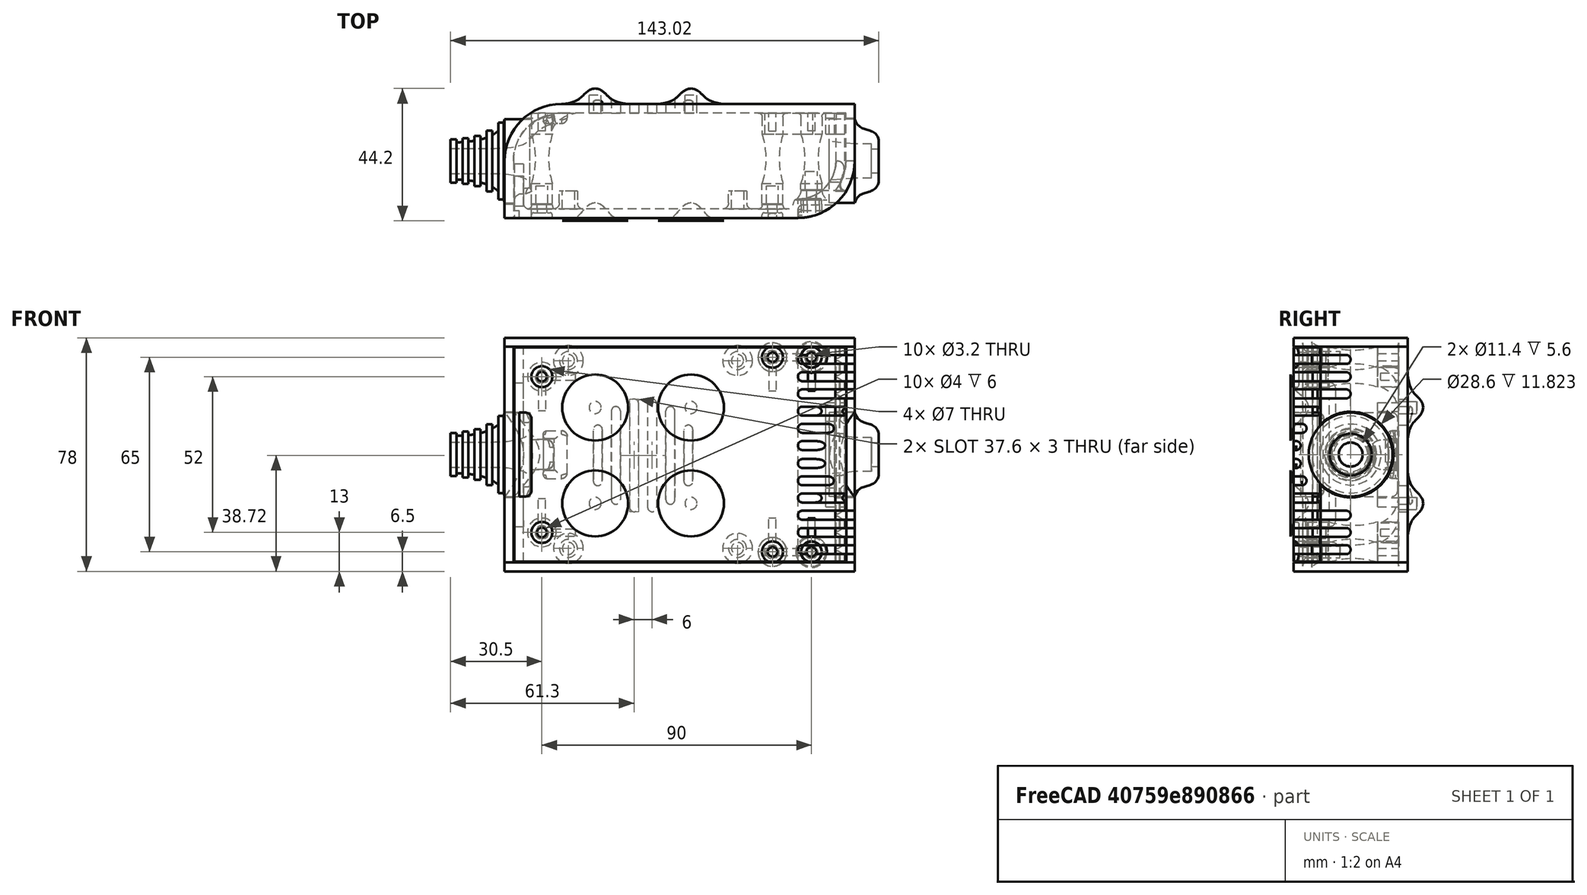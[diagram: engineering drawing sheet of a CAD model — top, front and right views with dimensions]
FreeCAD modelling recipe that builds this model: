
FCSTD DOCUMENT  (FreeCAD 0.19R0.19.2)
Label: enclosure_118
License: All rights reserved
LicenseURL: http://en.wikipedia.org/wiki/All_rights_reserved
objects: Part::Feature×72, Part::Revolution×72, Part::MultiFuse×53, Sketcher::SketchObject×32, Part::Fillet×24, Part::Cut×22, Part::Cylinder×22, Part::Extrusion×21, Part::Box×12, App::MeasureDistance×4
note: 330 computed .brp shape members not serialized (recipe doc carries the construction recipe); baked Part::Feature solids carry a one-line shape summary decoded from their .brp

FEATURE [Sketcher::SketchObject] Sketch  label="topSketch"
  FullyConstrained = true
  sketch-geometry (13):
    g0: LineSegment StartX=117 StartY=19 StartZ=0 EndX=117 EndY=38 EndZ=0
    g1: ArcOfCircle CenterX=98 CenterY=19 CenterZ=0 NormalX=0 NormalY=0 NormalZ=1 AngleXU=0 Radius=19 StartAngle=5.7297 EndAngle=6.28319
    g2: LineSegment StartX=0 StartY=3 StartZ=0 EndX=0 EndY=19 EndZ=0
    g3: LineSegment StartX=19 StartY=38 StartZ=0 EndX=117 EndY=38 EndZ=0
    g4: ArcOfCircle CenterX=19 CenterY=19 CenterZ=0 NormalX=0 NormalY=0 NormalZ=1 AngleXU=0 Radius=19 StartAngle=1.5708 EndAngle=3.14159
    g5: ArcOfCircle CenterX=19 CenterY=19 CenterZ=0 NormalX=0 NormalY=0 NormalZ=1 AngleXU=0 Radius=16 StartAngle=1.5708 EndAngle=3.14159
    g6: ArcOfCircle CenterX=98 CenterY=19 CenterZ=0 NormalX=0 NormalY=0 NormalZ=1 AngleXU=0 Radius=16 StartAngle=5.60905 EndAngle=6.28319
    g7: LineSegment StartX=114 StartY=19 StartZ=0 EndX=114 EndY=35 EndZ=0
    g8: LineSegment StartX=110.5 StartY=9.01251 StartZ=0 EndX=114.163 EndY=9.01251 EndZ=0
    g9: LineSegment StartX=114 StartY=35 StartZ=0 EndX=19 EndY=35 EndZ=0
    g10: LineSegment StartX=0 StartY=3 StartZ=0 EndX=0 EndY=0 EndZ=0
    g11: LineSegment StartX=3 StartY=0 StartZ=0 EndX=0 EndY=0 EndZ=0
    g12: LineSegment StartX=3 StartY=19 StartZ=0 EndX=3 EndY=0 EndZ=0
  constraints (33):
    c: Vertical(g0)
    c: Distance(g0) = 19
    c: Block(g0)
    c: Coincident(g1,g0)
    c: Block(g1)
    c: Vertical(g2)
    c: Block(g2)
    c: Coincident(g3,g0)
    c: Horizontal(g3)
    c: Distance(g3) = 98
    c: Coincident(g4,g3)
    c: Coincident(g4,g2)
    c: Block(g4)
    c: Coincident(g5,g4)
    c: Coincident(g6,g1)
    c: Block(g6)
    c: Block(g5)
    c: Coincident(g7,g6)
    c: Vertical(g7)
    c: Coincident(g8,g6)
    c: Coincident(g8,g1)
    c: Coincident(g9,g7)
    c: Coincident(g9,g5)
    c: Horizontal(g9)
    c: Tangent(g9,g5)
    c: Coincident(g10,g2)
    c: Distance(g10) = 3
    c: Vertical(g10)
    c: Coincident(g11,g10)
    c: Horizontal(g11)
    c: Coincident(g12,g5)
    c: Coincident(g12,g11)
    c: Vertical(g12)
FEATURE [Sketcher::SketchObject] Sketch001  label="bottomSketch"
  FullyConstrained = true
  sketch-geometry (32):
    g0: LineSegment StartX=3.3 StartY=-6.03275e-07 StartZ=0 EndX=98 EndY=-6.03275e-07 EndZ=0
    g1: ArcOfCircle CenterX=98 CenterY=19 CenterZ=0 NormalX=0 NormalY=0 NormalZ=1 AngleXU=0 Radius=19 StartAngle=4.71239 EndAngle=5.71103
    g2: LineSegment StartX=6.3 StartY=8 StartZ=0 EndX=3.3 EndY=8 EndZ=0
    g3: LineSegment StartX=3.3 StartY=8 StartZ=0 EndX=3.3 EndY=-6.03275e-07 EndZ=0
    g4: ArcOfCircle CenterX=8.3 CenterY=5 CenterZ=0 NormalX=0 NormalY=0 NormalZ=1 AngleXU=0 Radius=2 StartAngle=3.14159 EndAngle=4.71239
    g5: LineSegment StartX=6.3 StartY=8 StartZ=0 EndX=6.3 EndY=5 EndZ=0
    g6: ArcOfCircle CenterX=98 CenterY=19 CenterZ=0 NormalX=0 NormalY=0 NormalZ=1 AngleXU=0 Radius=12.7 StartAngle=4.71239 EndAngle=6.28319
    g7: LineSegment StartX=94.7 StartY=3 StartZ=0 EndX=8.3 EndY=3 EndZ=0
    g8-g12: Circle x5 (B-spline internal-alignment scaffolding for g13; pole/knot coordinates omitted)
    g13: BSplineCurve PolesCount=5 KnotsCount=3 Degree=3 IsPeriodic=0
    g14: GeomPoint X=98 Y=6.3 Z=0
    g15: GeomPoint X=96.3938 Y=4.71946 Z=0
    g16: GeomPoint X=94.7 Y=3 Z=0
    g17-g23: Circle x7 (B-spline internal-alignment scaffolding for g24; pole/knot coordinates omitted)
    g24: BSplineCurve PolesCount=7 KnotsCount=5 Degree=3 IsPeriodic=0
    g25-g29: GeomPoint x5 (B-spline internal-alignment scaffolding for g24; pole/knot coordinates omitted)
    g30: ArcOfCircle CenterX=98 CenterY=19 CenterZ=0 NormalX=0 NormalY=0 NormalZ=1 AngleXU=0 Radius=15.7 StartAngle=5.81226 EndAngle=6.28319
    g31: LineSegment StartX=110.7 StartY=19 StartZ=0 EndX=113.7 EndY=19 EndZ=0
  constraints (41):
    c: Horizontal(g0)
    c: Coincident(g1,g0)
    c: Block(g1)
    c: Horizontal(g2)
    c: Distance(g2) = 3
    c: Coincident(g3,g2)
    c: Vertical(g3)
    c: Coincident(g3,g0)
    c: Block(g4)
    c: Block(g2)
    c: Coincident(g5,g2)
    c: Coincident(g5,g4)
    c: Vertical(g5)
    c: Coincident(g6,g1)
    c: Block(g6)
    c: Coincident(g7,g4)
    c: Horizontal(g7)
    c: Block(g0)
    c: Block(g7)
    c: Block(g3)
    c: Coincident(g13,g6)
    c: Weight(g8) = 1
    c: Equal(g8, g9-g12) x4
    c: Coincident(g13,g7)
    c: InternalAlignment(g8-g12 -> g13) x5
    c: InternalAlignment(g14,g13)
    c: InternalAlignment(g15,g13)
    c: InternalAlignment(g16,g13)
    c: Block(g13)
    c: Weight(g17) = 1
    c: Equal(g17, g18-g23) x6
    c: Coincident(g24,g1)
    c: InternalAlignment(g17-g23 -> g24) x7
    c: InternalAlignment(g25-g29 -> g24) x5
    c: Block(g24)
    c: Coincident(g30,g24)
    c: Coincident(g31,g6)
    c: Coincident(g31,g30)
    c: Horizontal(g31)
    c: Block(g31)
    c: Block(g30)
FEATURE [Part::Extrusion] Extrude  label="top"
  Base = -> Sketch
  Dir = (0,0,1)
  DirMode = 2
  FaceMakerClass = Part::FaceMakerBullseye
  LengthFwd = 72
  LengthRev = 0
  Solid = true
  Symmetric = false
FEATURE [Part::Extrusion] Extrude001  label="bottom"
  Base = -> Sketch001
  Dir = (0,0,1)
  DirMode = 2
  FaceMakerClass = Part::FaceMakerBullseye
  LengthFwd = 71.4
  LengthRev = 0
  Placement = pos=(0,0,0.3) rot=(0,0,1;0rad)
  Solid = true
  Symmetric = false
FEATURE [Sketcher::SketchObject] Sketch002  label="topSketch001"
  FullyConstrained = true
  sketch-geometry (6):
    g0: LineSegment StartX=19 StartY=38 StartZ=0 EndX=117 EndY=38 EndZ=0
    g1: ArcOfCircle CenterX=19 CenterY=19 CenterZ=0 NormalX=0 NormalY=0 NormalZ=1 AngleXU=0 Radius=19 StartAngle=1.5708 EndAngle=3.14159
    g2: LineSegment StartX=117 StartY=38 StartZ=0 EndX=117 EndY=19 EndZ=0
    g3: LineSegment StartX=98 StartY=1.0161e-12 StartZ=0 EndX=5.22862e-06 EndY=1.0161e-12 EndZ=0
    g4: LineSegment StartX=5.22862e-06 StartY=19 StartZ=0 EndX=5.22862e-06 EndY=1.0161e-12 EndZ=0
    g5: ArcOfCircle CenterX=98 CenterY=19 CenterZ=0 NormalX=0 NormalY=0 NormalZ=1 AngleXU=0 Radius=19 StartAngle=4.71239 EndAngle=6.28319
  constraints (16):
    c: Horizontal(g0)
    c: Distance(g0) = 98
    c: Coincident(g1,g0)
    c: Block(g1)
    c: Coincident(g2,g0)
    c: Vertical(g2)
    c: Distance(g2) = 19
    c: Horizontal(g3)
    c: Coincident(g4,g1)
    c: Vertical(g4)
    c: Coincident(g3,g4)
    c: Block(g3)
    c: Coincident(g5,g2)
    c: Coincident(g5,g3)
    c: Block(g0)
    c: Block(g5)
FEATURE [Part::Extrusion] Extrude002  label="sideA"
  Base = -> Sketch002
  Dir = (0,0,1)
  DirMode = 2
  FaceMakerClass = Part::FaceMakerBullseye
  LengthFwd = 3
  LengthRev = 0
  Placement = pos=(0,0,-3) rot=(0,0,1;0rad)
  Solid = true
  Symmetric = false
FEATURE [Sketcher::SketchObject] Sketch003  label="topSketch002"
  FullyConstrained = true
  sketch-geometry (6):
    g0: LineSegment StartX=19 StartY=38 StartZ=0 EndX=117 EndY=38 EndZ=0
    g1: ArcOfCircle CenterX=19 CenterY=19 CenterZ=0 NormalX=0 NormalY=0 NormalZ=1 AngleXU=0 Radius=19 StartAngle=1.5708 EndAngle=3.14159
    g2: LineSegment StartX=117 StartY=38 StartZ=0 EndX=117 EndY=19 EndZ=0
    g3: LineSegment StartX=98 StartY=1.0161e-12 StartZ=0 EndX=5.22862e-06 EndY=1.0161e-12 EndZ=0
    g4: LineSegment StartX=5.22862e-06 StartY=19 StartZ=0 EndX=5.22862e-06 EndY=1.0161e-12 EndZ=0
    g5: ArcOfCircle CenterX=98 CenterY=19 CenterZ=0 NormalX=0 NormalY=0 NormalZ=1 AngleXU=0 Radius=19 StartAngle=4.71239 EndAngle=6.28319
  constraints (16):
    c: Horizontal(g0)
    c: Distance(g0) = 98
    c: Coincident(g1,g0)
    c: Block(g1)
    c: Coincident(g2,g0)
    c: Vertical(g2)
    c: Distance(g2) = 19
    c: Horizontal(g3)
    c: Coincident(g4,g1)
    c: Vertical(g4)
    c: Coincident(g3,g4)
    c: Block(g3)
    c: Coincident(g5,g2)
    c: Coincident(g5,g3)
    c: Block(g0)
    c: Block(g5)
FEATURE [Part::Extrusion] Extrude003  label="sideB"
  Base = -> Sketch003
  Dir = (0,0,1)
  DirMode = 2
  FaceMakerClass = Part::FaceMakerBullseye
  LengthFwd = 3
  LengthRev = 0
  Placement = pos=(0,0,72) rot=(0,0,1;0rad)
  Solid = true
  Symmetric = false
FEATURE [Sketcher::SketchObject] Sketch004
  FullyConstrained = true
  MapMode = 3
  Placement = pos=(0,0,0) rot=(1,0,0;1.5708rad)
  Support = -> [Extrude]
  sketch-geometry (8):
    g0: Circle CenterX=80.351 CenterY=-67.6202 CenterZ=0 NormalX=0 NormalY=0 NormalZ=1 AngleXU=0 Radius=2
    g1: Circle CenterX=80.351 CenterY=-67.6202 CenterZ=0 NormalX=0 NormalY=0 NormalZ=1 AngleXU=0 Radius=3
    g2: Circle CenterX=80.351 CenterY=-4.92017 CenterZ=0 NormalX=0 NormalY=0 NormalZ=1 AngleXU=0 Radius=2
    g3: Circle CenterX=80.351 CenterY=-4.92017 CenterZ=0 NormalX=0 NormalY=0 NormalZ=1 AngleXU=0 Radius=3
    g4: Circle CenterX=23.851 CenterY=-4.92017 CenterZ=0 NormalX=0 NormalY=0 NormalZ=1 AngleXU=0 Radius=2
    g5: Circle CenterX=23.851 CenterY=-4.92017 CenterZ=0 NormalX=0 NormalY=0 NormalZ=1 AngleXU=0 Radius=3
    g6: Circle CenterX=23.851 CenterY=-67.6202 CenterZ=0 NormalX=0 NormalY=0 NormalZ=1 AngleXU=0 Radius=2
    g7: Circle CenterX=23.851 CenterY=-67.6202 CenterZ=0 NormalX=0 NormalY=0 NormalZ=1 AngleXU=0 Radius=3
  constraints (8):
    c: Block(g3)
    c: Block(g2)
    c: Block(g1)
    c: Block(g0)
    c: Block(g6)
    c: Block(g7)
    c: Block(g4)
    c: Block(g5)
FEATURE [Part::Extrusion] Extrude004
  Base = -> Sketch004
  Dir = (0,-1,2e-16)
  DirMode = 2
  FaceMakerClass = Part::FaceMakerBullseye
  LengthFwd = 6
  LengthRev = 0
  Placement = pos=(0,9,0) rot=(0,0,1;0rad)
  Solid = true
  Symmetric = false
FEATURE [Sketcher::SketchObject] Sketch005
  FullyConstrained = true
  MapMode = 3
  Placement = pos=(0,0,0) rot=(1,0,0;1.5708rad)
  Support = -> [Extrude]
  sketch-geometry (8):
    g0: Circle CenterX=80.351 CenterY=-67.6202 CenterZ=0 NormalX=0 NormalY=0 NormalZ=1 AngleXU=0 Radius=3
    g1: Circle CenterX=80.351 CenterY=-4.92017 CenterZ=0 NormalX=0 NormalY=0 NormalZ=1 AngleXU=0 Radius=3
    g2: Circle CenterX=23.851 CenterY=-4.92017 CenterZ=0 NormalX=0 NormalY=0 NormalZ=1 AngleXU=0 Radius=3
    g3: Circle CenterX=23.851 CenterY=-67.6202 CenterZ=0 NormalX=0 NormalY=0 NormalZ=1 AngleXU=0 Radius=3
    g4: Circle CenterX=23.851 CenterY=-67.6202 CenterZ=0 NormalX=0 NormalY=0 NormalZ=1 AngleXU=0 Radius=5
    g5: Circle CenterX=80.351 CenterY=-67.6202 CenterZ=0 NormalX=0 NormalY=0 NormalZ=1 AngleXU=0 Radius=5
    g6: Circle CenterX=23.851 CenterY=-4.92017 CenterZ=0 NormalX=0 NormalY=0 NormalZ=1 AngleXU=0 Radius=5
    g7: Circle CenterX=80.351 CenterY=-4.92017 CenterZ=0 NormalX=0 NormalY=0 NormalZ=1 AngleXU=0 Radius=5
  constraints (8):
    c: Block(g1)
    c: Block(g0)
    c: Block(g3)
    c: Block(g2)
    c: Block(g5)
    c: Block(g4)
    c: Block(g6)
    c: Block(g7)
FEATURE [Part::Extrusion] Extrude005
  Base = -> Sketch005
  Dir = (0,-1,2e-16)
  DirMode = 2
  FaceMakerClass = Part::FaceMakerBullseye
  LengthFwd = 2
  LengthRev = 0
  Solid = true
  Symmetric = false
FEATURE [Sketcher::SketchObject] Sketch006
  FullyConstrained = true
  MapMode = 3
  Placement = pos=(0,0,0) rot=(1,0,0;1.5708rad)
  sketch-geometry (8):
    g0: Circle CenterX=80.351 CenterY=-67.6202 CenterZ=0 NormalX=0 NormalY=0 NormalZ=1 AngleXU=0 Radius=3
    g1: Circle CenterX=80.351 CenterY=-4.92017 CenterZ=0 NormalX=0 NormalY=0 NormalZ=1 AngleXU=0 Radius=3
    g2: Circle CenterX=23.851 CenterY=-4.92017 CenterZ=0 NormalX=0 NormalY=0 NormalZ=1 AngleXU=0 Radius=3
    g3: Circle CenterX=23.851 CenterY=-67.6202 CenterZ=0 NormalX=0 NormalY=0 NormalZ=1 AngleXU=0 Radius=3
    g4: Circle CenterX=23.851 CenterY=-67.6202 CenterZ=0 NormalX=0 NormalY=0 NormalZ=1 AngleXU=0 Radius=5
    g5: Circle CenterX=80.351 CenterY=-67.6202 CenterZ=0 NormalX=0 NormalY=0 NormalZ=1 AngleXU=0 Radius=5
    g6: Circle CenterX=23.851 CenterY=-4.92017 CenterZ=0 NormalX=0 NormalY=0 NormalZ=1 AngleXU=0 Radius=5
    g7: Circle CenterX=80.351 CenterY=-4.92017 CenterZ=0 NormalX=0 NormalY=0 NormalZ=1 AngleXU=0 Radius=5
  constraints (8):
    c: Block(g1)
    c: Block(g0)
    c: Block(g3)
    c: Block(g2)
    c: Block(g5)
    c: Block(g4)
    c: Block(g6)
    c: Block(g7)
FEATURE [Part::Extrusion] Extrude007
  Base = -> Sketch006
  Dir = (0,-1,2e-16)
  DirMode = 2
  FaceMakerClass = Part::FaceMakerBullseye
  LengthFwd = 2
  LengthRev = 0
  Solid = true
  Symmetric = false
FEATURE [Part::Fillet] Fillet
  Base = -> Extrude007
  Edges = 4 edges r=1.99: [Edge6,Edge12,Edge18,Edge24]
FEATURE [Part::Cut] Cut
  Base = -> Extrude005
  Placement = pos=(0,5,0) rot=(0,0,1;0rad)
  Tool = -> Fillet
FEATURE [Part::MultiFuse] Fusion  label="pCBScrews"
  Placement = pos=(-2.5,0,72.3) rot=(0,0,1;0rad)
  Shapes = -> [Extrude004,Cut]
FEATURE [App::MeasureDistance] Distance  label="Distance: 0.69 mm"
  Distance = 0.685967
  P1 = (24.0138,2.9647,0.3)
  P2 = (23.8901,3,-0.373787)
FEATURE [App::MeasureDistance] Distance001  label="Distance: 0.53 mm"
  Distance = 0.533607
  P1 = (80.2939,3,72.2334)
  P2 = (80.281,2.99661,71.7)
FEATURE [Part::Fillet] Fillet001
  Base = -> Extrude001
  Edges = 1 edges r=2.4: [Edge17]
FEATURE [Part::Fillet] Fillet002  label="bottom001"
  Base = -> Fillet001
  Edges = 1 edges r=2.4: [Edge36]
FEATURE [Part::Fillet] Fillet003  label="top001"
  Base = -> Extrude
  Edges = 1 edges r=2: [Edge1]
FEATURE [Sketcher::SketchObject] Sketch007
  FullyConstrained = true
  sketch-geometry (16):
    g0: LineSegment StartX=4 StartY=0 StartZ=0 EndX=4 EndY=2.4 EndZ=0
    g1: LineSegment StartX=4 StartY=2.4 StartZ=0 EndX=7 EndY=2.4 EndZ=0
    g2: LineSegment StartX=4 StartY=0 StartZ=0 EndX=5.7 EndY=0 EndZ=0
    g3: LineSegment StartX=5.7 StartY=0 StartZ=0 EndX=5.7 EndY=-5.6 EndZ=0
    g4-g8: Circle x5 (B-spline internal-alignment scaffolding for g9; pole/knot coordinates omitted)
    g9: BSplineCurve PolesCount=5 KnotsCount=3 Degree=3 IsPeriodic=0
    g10: GeomPoint X=7 Y=2.4 Z=0
    g11: GeomPoint X=10.4582 Y=-1.55472 Z=0
    g12: GeomPoint X=14 Y=-5.6 Z=0
    g13: LineSegment StartX=14 StartY=-5.6 StartZ=0 EndX=14 EndY=-14.1 EndZ=0
    g14: LineSegment StartX=14 StartY=-14.1 StartZ=0 EndX=6.5 EndY=-14.1 EndZ=0
    g15: LineSegment StartX=5.7 StartY=-5.6 StartZ=0 EndX=6.5 EndY=-14.1 EndZ=0
  constraints (28):
    c: Distance(g0) = 2.4
    c: Vertical(g0)
    c: Block(g0)
    c: Coincident(g1,g0)
    c: Horizontal(g1)
    c: Distance(g1) = 3
    c: Coincident(g2,g0)
    c: Horizontal(g2)
    c: Distance(g2) = 1.7
    c: Coincident(g3,g2)
    c: Vertical(g3)
    c: Distance(g3) = 5.6
    c: Coincident(g9,g1)
    c: Weight(g4) = 1
    c: Equal(g4, g5-g8) x4
    c: InternalAlignment(g4-g8 -> g9) x5
    c: InternalAlignment(g10,g9)
    c: InternalAlignment(g11,g9)
    c: InternalAlignment(g12,g9)
    c: Block(g9)
    c: Coincident(g13,g9)
    c: Vertical(g13)
    c: Distance(g13) = 8.5
    c: Coincident(g14,g13)
    c: Horizontal(g14)
    c: Distance(g14) = 7.5
    c: Coincident(g15,g3)
    c: Coincident(g15,g14)
FEATURE [Part::Feature] Face
  shape: bbox 10 x 16.5 x 2e-07 mm, 1 faces, 0 solids (baked)
FEATURE [Part::Revolution] Revolve  label="plugHousing"
  Angle = 360
  Axis = (0,1,0)
  Base = (0,0,0)
  FaceMakerClass = Part::FaceMakerBullseye
  Placement = pos=(0,0,36.15) rot=(0,0,1;0rad)
  Solid = false
  Source = -> Face
  Symmetric = false
FEATURE [Part::Feature] Face001
  shape: bbox 10 x 16.5 x 2e-07 mm, 1 faces, 0 solids (baked)
FEATURE [Part::Revolution] Revolve001  label="plugHousing001"
  Angle = 360
  Axis = (0,1,0)
  Base = (0,0,0)
  FaceMakerClass = Part::FaceMakerBullseye
  Placement = pos=(0,0,36.15) rot=(0,0,1;0rad)
  Solid = false
  Source = -> Face001
  Symmetric = false
FEATURE [Part::MultiFuse] Fusion001  label="plugHousing002"
  Placement = pos=(0,0,0) rot=(0,0,1;1.5708rad)
  Shapes = -> [Revolve001,Revolve]
FEATURE [Part::Feature] Face002
  shape: bbox 10 x 16.5 x 2e-07 mm, 1 faces, 0 solids (baked)
FEATURE [Part::Revolution] Revolve003  label="plugHousing005"
  Angle = 360
  Axis = (0,1,0)
  Base = (0,0,0)
  FaceMakerClass = Part::FaceMakerBullseye
  Placement = pos=(0,0,36.15) rot=(0,0,1;0rad)
  Solid = false
  Source = -> Face002
  Symmetric = false
FEATURE [Part::Feature] Face003
  shape: bbox 10 x 16.5 x 2e-07 mm, 1 faces, 0 solids (baked)
FEATURE [Part::Revolution] Revolve002  label="plugHousing003"
  Angle = 360
  Axis = (0,1,0)
  Base = (0,0,0)
  FaceMakerClass = Part::FaceMakerBullseye
  Placement = pos=(0,0,36.15) rot=(0,0,1;0rad)
  Solid = false
  Source = -> Face003
  Symmetric = false
FEATURE [Part::MultiFuse] Fusion002  label="plugHousing004"
  Placement = pos=(0,0,0) rot=(0,0,1;1.5708rad)
  Shapes = -> [Revolve002,Revolve003]
FEATURE [Part::MultiFuse] Fusion003  label="plugHousing006"
  Placement = pos=(0,19,0) rot=(0,0,1;3.14159rad)
  Shapes = -> [Fusion002,Fusion001]
FEATURE [Part::Feature] Face004
  shape: bbox 10 x 16.5 x 2e-07 mm, 1 faces, 0 solids (baked)
FEATURE [Part::Revolution] Revolve006  label="plugHousing010"
  Angle = 360
  Axis = (0,1,0)
  Base = (0,0,0)
  FaceMakerClass = Part::FaceMakerBullseye
  Placement = pos=(0,0,36.15) rot=(0,0,1;0rad)
  Solid = false
  Source = -> Face004
  Symmetric = false
FEATURE [Part::Feature] Face005
  shape: bbox 10 x 16.5 x 2e-07 mm, 1 faces, 0 solids (baked)
FEATURE [Part::Revolution] Revolve007  label="plugHousing011"
  Angle = 360
  Axis = (0,1,0)
  Base = (0,0,0)
  FaceMakerClass = Part::FaceMakerBullseye
  Placement = pos=(0,0,36.15) rot=(0,0,1;0rad)
  Solid = false
  Source = -> Face005
  Symmetric = false
FEATURE [Part::Feature] Face006
  shape: bbox 10 x 16.5 x 2e-07 mm, 1 faces, 0 solids (baked)
FEATURE [Part::Revolution] Revolve004  label="plugHousing007"
  Angle = 360
  Axis = (0,1,0)
  Base = (0,0,0)
  FaceMakerClass = Part::FaceMakerBullseye
  Placement = pos=(0,0,36.15) rot=(0,0,1;0rad)
  Solid = false
  Source = -> Face006
  Symmetric = false
FEATURE [Part::MultiFuse] Fusion004  label="plugHousing009"
  Placement = pos=(0,0,0) rot=(0,0,1;1.5708rad)
  Shapes = -> [Revolve004,Revolve007]
FEATURE [Part::Feature] Face007
  shape: bbox 10 x 16.5 x 2e-07 mm, 1 faces, 0 solids (baked)
FEATURE [Part::Revolution] Revolve005  label="plugHousing008"
  Angle = 360
  Axis = (0,1,0)
  Base = (0,0,0)
  FaceMakerClass = Part::FaceMakerBullseye
  Placement = pos=(0,0,36.15) rot=(0,0,1;0rad)
  Solid = false
  Source = -> Face007
  Symmetric = false
FEATURE [Part::MultiFuse] Fusion005  label="plugHousing012"
  Placement = pos=(0,0,0) rot=(0,0,1;1.5708rad)
  Shapes = -> [Revolve006,Revolve005]
FEATURE [Part::MultiFuse] Fusion006  label="plugHousing013"
  Placement = pos=(0,19,0) rot=(0,0,1;3.14159rad)
  Shapes = -> [Fusion005,Fusion004]
FEATURE [Part::MultiFuse] Fusion007  label="plugHousing014"
  Placement = pos=(122.621,0,-0.15) rot=(0,0,1;0rad)
  Shapes = -> [Fusion003,Fusion006]
FEATURE [Part::Cylinder] Cylinder002
  Angle = 360
  AttacherType = Attacher::AttachEngine3D
  Height = 20
  Placement = pos=(0,0,36.15) rot=(0,0,1;0rad)
  Radius = 4
FEATURE [Part::Cylinder] Cylinder003
  Angle = 360
  AttacherType = Attacher::AttachEngine3D
  Height = 10
  Placement = pos=(0,0,36.15) rot=(0,0,1;0rad)
  Radius = 4
FEATURE [Part::MultiFuse] Fusion009  label="removeToCreateHoleForPlugHousing"
  Placement = pos=(70,19,36.15) rot=(0,1,0;1.5708rad)
  Shapes = -> [Cylinder002,Cylinder003]
FEATURE [Part::Cylinder] Cylinder004
  Angle = 360
  AttacherType = Attacher::AttachEngine3D
  Height = 20
  Placement = pos=(0,0,36.15) rot=(0,0,1;0rad)
  Radius = 4
FEATURE [Part::Cylinder] Cylinder005
  Angle = 360
  AttacherType = Attacher::AttachEngine3D
  Height = 10
  Placement = pos=(0,0,36.15) rot=(0,0,1;0rad)
  Radius = 4
FEATURE [Part::MultiFuse] Fusion010  label="removeToCreateHoleForPlugHousing001"
  Placement = pos=(70,19,36.15) rot=(0,1,0;1.5708rad)
  Shapes = -> [Cylinder004,Cylinder005]
FEATURE [Part::Cut] Cut001
  Base = -> Fillet003
  Tool = -> Fusion010
FEATURE [Part::Cut] Cut002  label="Bottom"
  Base = -> Fillet002
  Tool = -> Fusion009
FEATURE [Part::Feature] Face008
  shape: bbox 10 x 16.5 x 2e-07 mm, 1 faces, 0 solids (baked)
FEATURE [Part::Revolution] Revolve011  label="plugHousing021"
  Angle = 360
  Axis = (0,1,0)
  Base = (0,0,0)
  FaceMakerClass = Part::FaceMakerBullseye
  Placement = pos=(0,0,36.15) rot=(0,0,1;0rad)
  Solid = false
  Source = -> Face008
  Symmetric = false
FEATURE [Part::Feature] Face009
  shape: bbox 10 x 16.5 x 2e-07 mm, 1 faces, 0 solids (baked)
FEATURE [Part::Revolution] Revolve012  label="plugHousing022"
  Angle = 360
  Axis = (0,1,0)
  Base = (0,0,0)
  FaceMakerClass = Part::FaceMakerBullseye
  Placement = pos=(0,0,36.15) rot=(0,0,1;0rad)
  Solid = false
  Source = -> Face009
  Symmetric = false
FEATURE [Part::Feature] Face010 .. Face013  x4 (patterned run collapsed; names and placements below)
  shape: bbox 10 x 16.5 x 2e-07 mm, 1 faces, 0 solids (baked)
FEATURE [Part::Revolution] Revolve015  label="plugHousing027"
  Angle = 360
  Axis = (0,1,0)
  Base = (0,0,0)
  FaceMakerClass = Part::FaceMakerBullseye
  Placement = pos=(0,0,36.15) rot=(0,0,1;0rad)
  Solid = false
  Source = -> Face013
  Symmetric = false
FEATURE [Part::Feature] Face014
  shape: bbox 10 x 16.5 x 2e-07 mm, 1 faces, 0 solids (baked)
FEATURE [Part::Feature] Face015
  shape: bbox 10 x 16.5 x 2e-07 mm, 1 faces, 0 solids (baked)
FEATURE [Part::Feature] Face016
  shape: bbox 10 x 16.5 x 2e-07 mm, 1 faces, 0 solids (baked)
FEATURE [Part::Revolution] Revolve019  label="plugHousing033"
  Angle = 360
  Axis = (0,1,0)
  Base = (0,0,0)
  FaceMakerClass = Part::FaceMakerBullseye
  Placement = pos=(0,0,36.15) rot=(0,0,1;0rad)
  Solid = false
  Source = -> Face016
  Symmetric = false
FEATURE [Part::Feature] Face017
  shape: bbox 10 x 16.5 x 2e-07 mm, 1 faces, 0 solids (baked)
FEATURE [Part::Revolution] Revolve020  label="plugHousing034"
  Angle = 360
  Axis = (0,1,0)
  Base = (0,0,0)
  FaceMakerClass = Part::FaceMakerBullseye
  Placement = pos=(0,0,36.15) rot=(0,0,1;0rad)
  Solid = false
  Source = -> Face017
  Symmetric = false
FEATURE [Part::Feature] Face018
  shape: bbox 10 x 16.5 x 2e-07 mm, 1 faces, 0 solids (baked)
FEATURE [Part::Revolution] Revolve016  label="plugHousing030"
  Angle = 360
  Axis = (0,1,0)
  Base = (0,0,0)
  FaceMakerClass = Part::FaceMakerBullseye
  Placement = pos=(0,0,36.15) rot=(0,0,1;0rad)
  Solid = false
  Source = -> Face018
  Symmetric = false
FEATURE [Part::MultiFuse] Fusion020  label="plugHousing038"
  Placement = pos=(0,0,0) rot=(0,0,1;1.5708rad)
  Shapes = -> [Revolve016,Revolve020]
FEATURE [Part::Feature] Face019
  shape: bbox 10 x 16.5 x 2e-07 mm, 1 faces, 0 solids (baked)
FEATURE [Part::Feature] Face020
  shape: bbox 10 x 16.5 x 2e-07 mm, 1 faces, 0 solids (baked)
FEATURE [Part::Revolution] Revolve017  label="plugHousing031"
  Angle = 360
  Axis = (0,1,0)
  Base = (0,0,0)
  FaceMakerClass = Part::FaceMakerBullseye
  Placement = pos=(0,0,36.15) rot=(0,0,1;0rad)
  Solid = false
  Source = -> Face020
  Symmetric = false
FEATURE [Part::MultiFuse] Fusion021  label="plugHousing039"
  Placement = pos=(0,0,0) rot=(0,0,1;1.5708rad)
  Shapes = -> [Revolve019,Revolve017]
FEATURE [Part::MultiFuse] Fusion023  label="plugHousing041"
  Placement = pos=(0,19,0) rot=(0,0,1;3.14159rad)
  Shapes = -> [Fusion021,Fusion020]
FEATURE [Part::Revolution] Revolve022  label="plugHousing043"
  Angle = 360
  Axis = (0,1,0)
  Base = (0,0,0)
  FaceMakerClass = Part::FaceMakerBullseye
  Placement = pos=(0,0,36.15) rot=(0,0,1;0rad)
  Solid = false
  Source = -> Face019
  Symmetric = false
FEATURE [Part::Feature] Face021
  shape: bbox 10 x 16.5 x 2e-07 mm, 1 faces, 0 solids (baked)
FEATURE [Part::Revolution] Revolve023  label="plugHousing044"
  Angle = 360
  Axis = (0,1,0)
  Base = (0,0,0)
  FaceMakerClass = Part::FaceMakerBullseye
  Placement = pos=(0,0,36.15) rot=(0,0,1;0rad)
  Solid = false
  Source = -> Face021
  Symmetric = false
FEATURE [Part::Feature] Face022
  shape: bbox 10 x 16.5 x 2e-07 mm, 1 faces, 0 solids (baked)
FEATURE [Part::Revolution] Revolve018  label="plugHousing032"
  Angle = 360
  Axis = (0,1,0)
  Base = (0,0,0)
  FaceMakerClass = Part::FaceMakerBullseye
  Placement = pos=(0,0,36.15) rot=(0,0,1;0rad)
  Solid = false
  Source = -> Face022
  Symmetric = false
FEATURE [Part::MultiFuse] Fusion022  label="plugHousing040"
  Placement = pos=(0,0,0) rot=(0,0,1;1.5708rad)
  Shapes = -> [Revolve018,Revolve023]
FEATURE [Part::Feature] Face023
  shape: bbox 10 x 16.5 x 2e-07 mm, 1 faces, 0 solids (baked)
FEATURE [Part::Revolution] Revolve021  label="plugHousing035"
  Angle = 360
  Axis = (0,1,0)
  Base = (0,0,0)
  FaceMakerClass = Part::FaceMakerBullseye
  Placement = pos=(0,0,36.15) rot=(0,0,1;0rad)
  Solid = false
  Source = -> Face023
  Symmetric = false
FEATURE [Part::MultiFuse] Fusion018  label="plugHousing036"
  Placement = pos=(0,0,0) rot=(0,0,1;1.5708rad)
  Shapes = -> [Revolve022,Revolve021]
FEATURE [Part::MultiFuse] Fusion019  label="plugHousing037"
  Placement = pos=(0,19,0) rot=(0,0,1;3.14159rad)
  Shapes = -> [Fusion018,Fusion022]
FEATURE [Part::MultiFuse] Fusion024  label="plugHousing042"
  Placement = pos=(122.621,0,-0.15) rot=(0,0,1;0rad)
  Shapes = -> [Fusion023,Fusion019]
FEATURE [Part::Cylinder] Cylinder006
  Angle = 360
  AttacherType = Attacher::AttachEngine3D
  Height = 20
  Placement = pos=(0,0,36.15) rot=(0,0,1;0rad)
  Radius = 14.3
FEATURE [Part::Cylinder] Cylinder007
  Angle = 360
  AttacherType = Attacher::AttachEngine3D
  Height = 10
  Placement = pos=(0,0,36.15) rot=(0,0,1;0rad)
  Radius = 4
FEATURE [Part::MultiFuse] Fusion026  label="removeToCreteHoleForPlugHousing"
  Placement = pos=(70,19,36) rot=(0,1,0;1.5708rad)
  Shapes = -> [Cylinder006,Cylinder007]
FEATURE [Part::Box] Box001  label="Cube001"
  AttacherType = Attacher::AttachEngine3D
  Height = 28
  Length = 3
  Placement = pos=(110.7,19,22) rot=(0,0,1;0rad)
  Width = 15.7
FEATURE [Part::Cut] Cut003  label="top002"
  Base = -> Cut001
  Tool = -> Fusion007
FEATURE [Part::Revolution] Revolve008  label="plugHousing015"
  Angle = 360
  Axis = (0,1,0)
  Base = (0,0,0)
  FaceMakerClass = Part::FaceMakerBullseye
  Placement = pos=(0,0,36.15) rot=(0,0,1;0rad)
  Solid = false
  Source = -> Face010
  Symmetric = false
FEATURE [Part::MultiFuse] Fusion013  label="plugHousing020"
  Placement = pos=(0,0,0) rot=(0,0,1;1.5708rad)
  Shapes = -> [Revolve008,Revolve012]
FEATURE [Part::Cut] Cut004  label="top003"
  Base = -> Cut003
  Placement = pos=(1,0,0) rot=(0,0,1;0rad)
  Tool = -> Fusion026
FEATURE [Part::Cylinder] Cylinder008
  Angle = 360
  AttacherType = Attacher::AttachEngine3D
  Height = 20
  Placement = pos=(0,0,36.15) rot=(0,0,1;0rad)
  Radius = 10.3
FEATURE [Part::Cylinder] Cylinder009
  Angle = 360
  AttacherType = Attacher::AttachEngine3D
  Height = 10
  Placement = pos=(0,0,36.15) rot=(0,0,1;0rad)
  Radius = 4
FEATURE [Part::MultiFuse] Fusion027  label="removeToCreteHoleForPlugHousing001"
  Placement = pos=(70,19,36) rot=(0,1,0;1.5708rad)
  Shapes = -> [Cylinder008,Cylinder009]
FEATURE [Part::Cut] Cut005  label="plugHousingTab"
  Base = -> Box001
  Tool = -> Fusion027
FEATURE [Part::MultiFuse] Fusion028  label="plugHousing045"
  Shapes = -> [Fusion024,Cut005]
FEATURE [Part::Box] Box002  label="Cube002"
  AttacherType = Attacher::AttachEngine3D
  Height = 28.8
  Length = 3
  Placement = pos=(107.3,28,21.6) rot=(0,0,1;0rad)
  Width = 7
FEATURE [Part::Box] Box003  label="Cube003"
  AttacherType = Attacher::AttachEngine3D
  Height = 3
  Length = 6.4
  Placement = pos=(107.3,28,18.6) rot=(0,0,1;0rad)
  Width = 7
FEATURE [Part::Box] Box004  label="Cube004"
  AttacherType = Attacher::AttachEngine3D
  Height = 3
  Length = 6.4
  Placement = pos=(107.3,28,50.4) rot=(0,0,1;0rad)
  Width = 7
FEATURE [Part::MultiFuse] Fusion029  label="plugHousingBracketHolder"
  Shapes = -> [Box004,Box002,Box003]
FEATURE [Part::Cylinder] Cylinder010
  Angle = 360
  AttacherType = Attacher::AttachEngine3D
  Height = 20
  Placement = pos=(0,0,36.15) rot=(0,0,1;0rad)
  Radius = 14.3
FEATURE [Part::Cylinder] Cylinder011
  Angle = 360
  AttacherType = Attacher::AttachEngine3D
  Height = 10
  Placement = pos=(0,0,36.15) rot=(0,0,1;0rad)
  Radius = 4
FEATURE [Part::MultiFuse] Fusion030  label="removeToCreteHoleForPlugHousing002"
  Placement = pos=(70,19,36) rot=(0,1,0;1.5708rad)
  Shapes = -> [Cylinder010,Cylinder011]
FEATURE [Part::Cut] Cut006  label="plugHousingBracketHolder001"
  Base = -> Fusion029
  Tool = -> Fusion030
FEATURE [Part::Cylinder] Cylinder012
  Angle = 360
  AttacherType = Attacher::AttachEngine3D
  Height = 20
  Placement = pos=(0,0,36.15) rot=(0,0,1;0rad)
  Radius = 7
FEATURE [Part::Cylinder] Cylinder013
  Angle = 360
  AttacherType = Attacher::AttachEngine3D
  Height = 10
  Placement = pos=(0,0,36.15) rot=(0,0,1;0rad)
  Radius = 4
FEATURE [Part::MultiFuse] Fusion032  label="removeToCreteHoleForPlugHousing003"
  Placement = pos=(70,19,36) rot=(0,1,0;1.5708rad)
  Shapes = -> [Cylinder012,Cylinder013]
FEATURE [Part::Cut] Cut007  label="bottom002"
  Base = -> Cut002
  Tool = -> Fusion032
FEATURE [Sketcher::SketchObject] Sketch008
  FullyConstrained = true
  sketch-geometry (54):
    g0: LineSegment StartX=-4.2 StartY=0 StartZ=0 EndX=-6.2 EndY=0 EndZ=0
    g1: LineSegment StartX=-14 StartY=-18 StartZ=0 EndX=-14 EndY=-26.5 EndZ=0
    g2: LineSegment StartX=-4.2 StartY=0 StartZ=0 EndX=-4.2 EndY=-13.4877 EndZ=0
    g3: Circle CenterX=-4.2 CenterY=-13.4877 CenterZ=0 NormalX=0 NormalY=0 NormalZ=1 AngleXU=0 Radius=1
    g4: Circle CenterX=-4.2 CenterY=-26.5 CenterZ=0 NormalX=0 NormalY=0 NormalZ=1 AngleXU=0 Radius=1
    g5: Circle CenterX=-8.2 CenterY=-26.5 CenterZ=0 NormalX=0 NormalY=0 NormalZ=1 AngleXU=0 Radius=1
    g6: BSplineCurve PolesCount=3 KnotsCount=2 Degree=2 IsPeriodic=0
    g7: GeomPoint X=-4.2 Y=-13.4877 Z=0
    g8: GeomPoint X=-8.2 Y=-26.5 Z=0
    g9: LineSegment StartX=-14 StartY=-26.5 StartZ=0 EndX=-8.2 EndY=-26.5 EndZ=0
    g10: LineSegment StartX=-10.15 StartY=-12 StartZ=0 EndX=-10.15 EndY=-14 EndZ=0
    g11: LineSegment StartX=-12.8401 StartY=-16 StartZ=0 EndX=-10.1571 EndY=-16 EndZ=0
    g12: LineSegment StartX=-10.15 StartY=-14 StartZ=0 EndX=-8.70761 EndY=-14 EndZ=0
    g13: LineSegment StartX=-12.8401 StartY=-16 StartZ=0 EndX=-12.8401 EndY=-17.6958 EndZ=0
    g14: LineSegment StartX=-10.15 StartY=-12 StartZ=0 EndX=-7.79258 EndY=-12 EndZ=0
    g15: Circle CenterX=-6.2215 CenterY=-2 CenterZ=0 NormalX=0 NormalY=0 NormalZ=1 AngleXU=0 Radius=1
    g16: Circle CenterX=-6.22762 CenterY=-2.58724 CenterZ=0 NormalX=0 NormalY=0 NormalZ=1 AngleXU=0 Radius=1
    g17: Circle CenterX=-6.32538 CenterY=-4 CenterZ=0 NormalX=0 NormalY=0 NormalZ=1 AngleXU=0 Radius=1
    g18: BSplineCurve PolesCount=3 KnotsCount=2 Degree=2 IsPeriodic=0
    g19: GeomPoint X=-6.2215 Y=-2 Z=0
    g20: GeomPoint X=-6.32538 Y=-4 Z=0
    g21: Circle CenterX=-6.48644 CenterY=-5.99526 CenterZ=0 NormalX=0 NormalY=0 NormalZ=1 AngleXU=0 Radius=1
    g22: Circle CenterX=-6.58486 CenterY=-6.99526 CenterZ=0 NormalX=0 NormalY=0 NormalZ=1 AngleXU=0 Radius=1
    g23: Circle CenterX=-6.77343 CenterY=-8 CenterZ=0 NormalX=0 NormalY=0 NormalZ=1 AngleXU=0 Radius=1
    g24: BSplineCurve PolesCount=3 KnotsCount=2 Degree=2 IsPeriodic=0
    g25: GeomPoint X=-6.48644 Y=-5.99526 Z=0
    g26: GeomPoint X=-6.77343 Y=-8 Z=0
    g27: Circle CenterX=-7.19003 CenterY=-10 CenterZ=0 NormalX=0 NormalY=0 NormalZ=1 AngleXU=0 Radius=1
    g28: Circle CenterX=-7.44407 CenterY=-11.0915 CenterZ=0 NormalX=0 NormalY=0 NormalZ=1 AngleXU=0 Radius=1
    g29: Circle CenterX=-7.79258 CenterY=-12 CenterZ=0 NormalX=0 NormalY=0 NormalZ=1 AngleXU=0 Radius=1
    g30: BSplineCurve PolesCount=3 KnotsCount=2 Degree=2 IsPeriodic=0
    g31: GeomPoint X=-7.19003 Y=-10 Z=0
    g32: GeomPoint X=-7.79258 Y=-12 Z=0
    g33: Circle CenterX=-8.70761 CenterY=-14 CenterZ=0 NormalX=0 NormalY=0 NormalZ=1 AngleXU=0 Radius=1
    g34: Circle CenterX=-9.33087 CenterY=-15.1837 CenterZ=0 NormalX=0 NormalY=0 NormalZ=1 AngleXU=0 Radius=1
    g35: Circle CenterX=-10.1571 CenterY=-16 CenterZ=0 NormalX=0 NormalY=0 NormalZ=1 AngleXU=0 Radius=1
    g36: BSplineCurve PolesCount=3 KnotsCount=2 Degree=2 IsPeriodic=0
    g37: GeomPoint X=-8.70761 Y=-14 Z=0
    g38: GeomPoint X=-10.1571 Y=-16 Z=0
    g39: Circle CenterX=-12.8401 CenterY=-17.6958 CenterZ=0 NormalX=0 NormalY=0 NormalZ=1 AngleXU=0 Radius=1
    g40: Circle CenterX=-13.3521 CenterY=-17.9027 CenterZ=0 NormalX=0 NormalY=0 NormalZ=1 AngleXU=0 Radius=1
    g41: Circle CenterX=-14 CenterY=-18 CenterZ=0 NormalX=0 NormalY=0 NormalZ=1 AngleXU=0 Radius=1
    g42: BSplineCurve PolesCount=3 KnotsCount=2 Degree=2 IsPeriodic=0
    g43: GeomPoint X=-12.8401 Y=-17.6958 Z=0
    g44: GeomPoint X=-14 Y=-18 Z=0
    g45: LineSegment StartX=-6.2 StartY=0 StartZ=0 EndX=-7.2 EndY=0 EndZ=0
    g46: LineSegment StartX=-7.2 StartY=0 StartZ=0 EndX=-7.2 EndY=-2 EndZ=0
    g47: LineSegment StartX=-7.2 StartY=-2 StartZ=0 EndX=-6.2215 EndY=-2 EndZ=0
    g48: LineSegment StartX=-6.32538 StartY=-4 StartZ=0 EndX=-7.65538 EndY=-4 EndZ=0
    g49: LineSegment StartX=-7.65538 StartY=-4 StartZ=0 EndX=-7.65538 EndY=-5.99526 EndZ=0
    g50: LineSegment StartX=-7.65538 StartY=-5.99526 StartZ=0 EndX=-6.48644 EndY=-5.99526 EndZ=0
    g51: LineSegment StartX=-6.77343 StartY=-8 StartZ=0 EndX=-8.43343 EndY=-8 EndZ=0
    g52: LineSegment StartX=-8.43343 StartY=-8 StartZ=0 EndX=-8.43343 EndY=-10 EndZ=0
    g53: LineSegment StartX=-8.43343 StartY=-10 StartZ=0 EndX=-7.19003 EndY=-10 EndZ=0
  constraints (112):
    c: Horizontal(g0)
    c: Distance(g0) = 2
    c: Block(g0)
    c: Vertical(g1)
    c: Coincident(g2,g0)
    c: Vertical(g2)
    c: Block(g2)
    c: Coincident(g6,g2)
    c: Weight(g3) = 1
    c: Equal(g3,g4)
    c: Equal(g3,g5)
    c: InternalAlignment(g3,g6)
    c: InternalAlignment(g4,g6)
    c: InternalAlignment(g5,g6)
    c: InternalAlignment(g7,g6)
    c: InternalAlignment(g8,g6)
    c: Block(g6)
    c: Coincident(g9,g1)
    c: Coincident(g9,g6)
    c: Horizontal(g9)
    c: Vertical(g10)
    c: Block(g10)
    c: Horizontal(g11)
    c: Block(g11)
    c: Coincident(g12,g10)
    c: Horizontal(g12)
    c: Block(g12)
    c: Coincident(g13,g11)
    c: Vertical(g13)
    c: Block(g13)
    c: Coincident(g14,g10)
    c: Horizontal(g14)
    c: Block(g14)
    c: Block(g9)
    c: Block(g1)
    c: Weight(g15) = 1
    c: Equal(g15,g16)
    c: Equal(g15,g17)
    c: InternalAlignment(g15,g18)
    c: InternalAlignment(g16,g18)
    c: InternalAlignment(g17,g18)
    c: InternalAlignment(g19,g18)
    c: InternalAlignment(g20,g18)
    c: Weight(g21) = 1
    c: Equal(g21,g22)
    c: Equal(g21,g23)
    c: InternalAlignment(g21,g24)
    c: InternalAlignment(g22,g24)
    c: InternalAlignment(g23,g24)
    c: InternalAlignment(g25,g24)
    c: InternalAlignment(g26,g24)
    c: Weight(g27) = 1
    c: Equal(g27,g28)
    c: Equal(g27,g29)
    c: Coincident(g30,g14)
    c: InternalAlignment(g27,g30)
    c: InternalAlignment(g28,g30)
    c: InternalAlignment(g29,g30)
    c: InternalAlignment(g31,g30)
    c: InternalAlignment(g32,g30)
    c: Coincident(g36,g12)
    c: Weight(g33) = 1
    c: Equal(g33,g34)
    c: Equal(g33,g35)
    c: Coincident(g36,g11)
    c: InternalAlignment(g33,g36)
    c: InternalAlignment(g34,g36)
    c: InternalAlignment(g35,g36)
    c: InternalAlignment(g37,g36)
    c: InternalAlignment(g38,g36)
    c: Coincident(g42,g13)
    c: Weight(g39) = 1
    c: Equal(g39,g40)
    c: Equal(g39,g41)
    c: Coincident(g42,g1)
    c: InternalAlignment(g39,g42)
    c: InternalAlignment(g40,g42)
    c: InternalAlignment(g41,g42)
    c: InternalAlignment(g43,g42)
    c: InternalAlignment(g44,g42)
    c: Block(g18)
    c: Block(g24)
    c: Block(g30)
    c: Block(g36)
    c: Block(g42)
    c: Horizontal(g45)
    c: Coincident(g45,g0)
    c: Vertical(g46)
    c: Coincident(g46,g45)
    c: Coincident(g47,g46)
    c: Coincident(g47,g18)
    c: Horizontal(g47)
    c: Block(g46)
    c: Coincident(g48,g18)
    c: Horizontal(g48)
    c: Distance(g48) = 1.33
    c: Vertical(g49)
    c: Coincident(g49,g48)
    c: Coincident(g50,g49)
    c: Coincident(g50,g24)
    c: Horizontal(g50)
    c: Tangent(g50,g22)
    c: Horizontal(g51)
    c: Coincident(g51,g24)
    c: Block(g51)
    c: Vertical(g52)
    c: Block(g52)
    c: Coincident(g52,g51)
    c: Coincident(g53,g52)
    c: Coincident(g53,g30)
    c: Horizontal(g53)
    c: Distance(g1) = 8.5
FEATURE [Part::Feature] Face024
  shape: bbox 9.8 x 26.5 x 2e-07 mm, 1 faces, 0 solids (baked)
FEATURE [Part::Revolution] Revolve024
  Angle = 360
  Axis = (0,1,0)
  Base = (0,0,0)
  FaceMakerClass = Part::FaceMakerBullseye
  Placement = pos=(0,0,0) rot=(0,0,1;1.5708rad)
  Solid = false
  Source = -> Face024
  Symmetric = false
FEATURE [Part::Feature] Face025
  shape: bbox 9.8 x 26.5 x 2e-07 mm, 1 faces, 0 solids (baked)
FEATURE [Part::Revolution] Revolve025
  Angle = 360
  Axis = (0,1,0)
  Base = (0,0,0)
  FaceMakerClass = Part::FaceMakerBullseye
  Placement = pos=(0,0,0) rot=(0,0,1;1.5708rad)
  Solid = false
  Source = -> Face025
  Symmetric = false
FEATURE [Part::MultiFuse] Fusion033
  Placement = pos=(-18,19,36) rot=(0,0,1;0rad)
  Shapes = -> [Revolve025,Revolve024]
FEATURE [Part::Cylinder] Cylinder014
  Angle = 360
  AttacherType = Attacher::AttachEngine3D
  Height = 20
  Placement = pos=(0,0,36.15) rot=(0,0,1;0rad)
  Radius = 14.3
FEATURE [Part::Cylinder] Cylinder015
  Angle = 360
  AttacherType = Attacher::AttachEngine3D
  Height = 10
  Placement = pos=(0,0,36.15) rot=(0,0,1;0rad)
  Radius = 4
FEATURE [Part::MultiFuse] Fusion034  label="removeToCreteHoleForPlugHousing004"
  Placement = pos=(-42,19,36) rot=(0,1,0;1.5708rad)
  Shapes = -> [Cylinder014,Cylinder015]
FEATURE [Part::Cut] Cut008  label="top004"
  Base = -> Cut004
  Placement = pos=(-1,0,0) rot=(0,0,1;0rad)
  Tool = -> Fusion034
FEATURE [Part::Box] Box005  label="Cube005"
  AttacherType = Attacher::AttachEngine3D
  Height = 28
  Length = 3
  Placement = pos=(110.7,19,22) rot=(0,0,1;0rad)
  Width = 15.7
FEATURE [Part::Cylinder] Cylinder016
  Angle = 360
  AttacherType = Attacher::AttachEngine3D
  Height = 10
  Placement = pos=(0,0,36.15) rot=(0,0,1;0rad)
  Radius = 4
FEATURE [Part::Cylinder] Cylinder017
  Angle = 360
  AttacherType = Attacher::AttachEngine3D
  Height = 20
  Placement = pos=(0,0,36.15) rot=(0,0,1;0rad)
  Radius = 10.3
FEATURE [Part::MultiFuse] Fusion035  label="removeToCreteHoleForPlugHousing005"
  Placement = pos=(70,19,36) rot=(0,1,0;1.5708rad)
  Shapes = -> [Cylinder017,Cylinder016]
FEATURE [Part::Cut] Cut009  label="plugHousingTab001"
  Base = -> Box005
  Placement = pos=(-107.4,-14,0) rot=(0,0,1;0rad)
  Tool = -> Fusion035
FEATURE [Part::Box] Box006  label="Cube006"
  AttacherType = Attacher::AttachEngine3D
  Height = 28
  Length = 3
  Placement = pos=(110.7,19,22) rot=(0,0,1;0rad)
  Width = 15.7
FEATURE [Part::Cylinder] Cylinder018
  Angle = 360
  AttacherType = Attacher::AttachEngine3D
  Height = 10
  Placement = pos=(0,0,36.15) rot=(0,0,1;0rad)
  Radius = 4
FEATURE [Part::Cylinder] Cylinder019
  Angle = 360
  AttacherType = Attacher::AttachEngine3D
  Height = 20
  Placement = pos=(0,0,36.15) rot=(0,0,1;0rad)
  Radius = 10.3
FEATURE [Part::MultiFuse] Fusion036  label="removeToCreteHoleForPlugHousing006"
  Placement = pos=(70,19,36) rot=(0,1,0;1.5708rad)
  Shapes = -> [Cylinder019,Cylinder018]
FEATURE [Part::Cut] Cut010  label="plugHousingTab002"
  Base = -> Box006
  Placement = pos=(-107.4,-14,0) rot=(0,0,1;0rad)
  Tool = -> Fusion036
FEATURE [Part::MultiFuse] Fusion037
  Placement = pos=(9.6,23,0) rot=(0,0,1;3.14159rad)
  Shapes = -> [Cut009,Cut010]
FEATURE [Part::Box] Box  label="Cube"
  AttacherType = Attacher::AttachEngine3D
  Height = 10
  Length = 3
  Placement = pos=(3.3,4,12) rot=(0,0,1;0rad)
  Width = 10
FEATURE [Part::Fillet] Fillet004
  Base = -> Fusion028
  Edges = 1 edges r=2: [Edge25]
FEATURE [Part::Fillet] Fillet005  label="plugHousing046"
  Base = -> Fillet004
  Edges = 1 edges r=2: [Edge8]
FEATURE [Part::Fillet] Fillet006
  Base = -> Box
  Edges = 1 edges r=2: [Edge11]
FEATURE [Part::Box] Box007  label="Cube007"
  AttacherType = Attacher::AttachEngine3D
  Height = 10
  Length = 3
  Placement = pos=(3.3,4,50) rot=(0,0,1;0rad)
  Width = 10
FEATURE [Part::Fillet] Fillet007
  Base = -> Box007
  Edges = 1 edges r=2: [Edge12]
FEATURE [Part::Box] Box008  label="Cube008"
  AttacherType = Attacher::AttachEngine3D
  Height = 28
  Length = 4
  Placement = pos=(5,0,22) rot=(0,0,1;0rad)
  Width = 10
FEATURE [Part::Fillet] Fillet008
  Base = -> Box008
  Edges = 1 edges r=1: [Edge7]
FEATURE [Part::Fillet] Fillet009
  Base = -> Fillet008
  Edges = 1 edges r=2: [Edge5]
FEATURE [Part::Fillet] Fillet010
  Base = -> Fillet009
  Edges = 1 edges r=2: [Edge2]
FEATURE [Sketcher::SketchObject] Sketch009  label="topSketch003"
  FullyConstrained = true
  sketch-geometry (4):
    g0: LineSegment StartX=16.8446 StartY=31.512 StartZ=0 EndX=16.3251 EndY=34.4666 EndZ=0
    g1: ArcOfCircle CenterX=19 CenterY=19.2524 CenterZ=0 NormalX=0 NormalY=0 NormalZ=1 AngleXU=0 Radius=15.4476 StartAngle=1.74483 EndAngle=2.72717
    g2: ArcOfCircle CenterX=19 CenterY=19.2524 CenterZ=0 NormalX=0 NormalY=0 NormalZ=1 AngleXU=0 Radius=12.4476 StartAngle=1.74483 EndAngle=2.73189
    g3: LineSegment StartX=4.86004 StartY=25.4725 StartZ=0 EndX=7.58253 EndY=24.2107 EndZ=0
  constraints (7):
    c: Block(g0)
    c: Coincident(g1,g0)
    c: Coincident(g2,g0)
    c: Coincident(g3,g1)
    c: Coincident(g3,g2)
    c: Block(g1)
    c: Block(g2)
FEATURE [Part::Extrusion] Extrude008
  Base = -> Sketch009
  Dir = (0,0,1)
  DirMode = 2
  FaceMakerClass = Part::FaceMakerBullseye
  LengthFwd = 10
  LengthRev = 0
  Placement = pos=(0,0,31) rot=(0,0,1;0rad)
  Solid = true
  Symmetric = false
FEATURE [Part::Cylinder] Cylinder020
  Angle = 360
  AttacherType = Attacher::AttachEngine3D
  Height = 20
  Placement = pos=(0,0,36.15) rot=(0,0,1;0rad)
  Radius = 8.2
FEATURE [Part::Cylinder] Cylinder021
  Angle = 360
  AttacherType = Attacher::AttachEngine3D
  Height = 10
  Placement = pos=(0,0,36.15) rot=(0,0,1;0rad)
  Radius = 4
FEATURE [Part::MultiFuse] Fusion038  label="removeToCreteHoleForPlugHousing007"
  Placement = pos=(-42,19,36) rot=(0,1,0;1.5708rad)
  Shapes = -> [Cylinder020,Cylinder021]
FEATURE [Part::Cut] Cut011
  Base = -> Extrude008
  Tool = -> Fusion038
FEATURE [Part::Fillet] Fillet011
  Base = -> Cut011
  Edges = 1 edges r=2: [Edge1]
FEATURE [Part::Fillet] Fillet012
  Base = -> Fillet011
  Edges = 1 edges r=2.5: [Edge1]
FEATURE [Part::Fillet] Fillet013
  Base = -> Fillet012
  Edges = 1 edges r=2.5: [Edge2]
FEATURE [Part::Box] Box010  label="Cube010"
  AttacherType = Attacher::AttachEngine3D
  Height = 16
  Length = 8
  Placement = pos=(12.7,31.52,28) rot=(0,0,1;0rad)
  Width = 4
FEATURE [Sketcher::SketchObject] Sketch010  label="topSketch004"
  FullyConstrained = true
  sketch-geometry (4):
    g0: LineSegment StartX=16.8446 StartY=31.512 StartZ=0 EndX=16.3251 EndY=34.4666 EndZ=0
    g1: ArcOfCircle CenterX=19 CenterY=19.2524 CenterZ=0 NormalX=0 NormalY=0 NormalZ=1 AngleXU=0 Radius=15.4476 StartAngle=1.74483 EndAngle=2.72717
    g2: ArcOfCircle CenterX=19 CenterY=19.2524 CenterZ=0 NormalX=0 NormalY=0 NormalZ=1 AngleXU=0 Radius=12.4476 StartAngle=1.74483 EndAngle=2.73189
    g3: LineSegment StartX=4.86004 StartY=25.4725 StartZ=0 EndX=7.58253 EndY=24.2107 EndZ=0
  constraints (7):
    c: Block(g0)
    c: Coincident(g1,g0)
    c: Coincident(g2,g0)
    c: Coincident(g3,g1)
    c: Coincident(g3,g2)
    c: Block(g1)
    c: Block(g2)
FEATURE [Part::Cylinder] Cylinder022
  Angle = 360
  AttacherType = Attacher::AttachEngine3D
  Height = 10
  Placement = pos=(0,0,36.15) rot=(0,0,1;0rad)
  Radius = 4
FEATURE [Sketcher::SketchObject] Sketch011  label="topSketch005"
  FullyConstrained = true
  sketch-geometry (4):
    g0: LineSegment StartX=16.8446 StartY=31.512 StartZ=0 EndX=16.3251 EndY=34.4666 EndZ=0
    g1: ArcOfCircle CenterX=19 CenterY=19.2524 CenterZ=0 NormalX=0 NormalY=0 NormalZ=1 AngleXU=0 Radius=15.4476 StartAngle=1.74483 EndAngle=2.72717
    g2: ArcOfCircle CenterX=19 CenterY=19.2524 CenterZ=0 NormalX=0 NormalY=0 NormalZ=1 AngleXU=0 Radius=12.4476 StartAngle=1.74483 EndAngle=2.73189
    g3: LineSegment StartX=4.86004 StartY=25.4725 StartZ=0 EndX=7.58253 EndY=24.2107 EndZ=0
  constraints (7):
    c: Block(g0)
    c: Coincident(g1,g0)
    c: Coincident(g2,g0)
    c: Coincident(g3,g1)
    c: Coincident(g3,g2)
    c: Block(g1)
    c: Block(g2)
FEATURE [Part::Extrusion] Extrude010
  Base = -> Sketch011
  Dir = (0,0,1)
  DirMode = 2
  FaceMakerClass = Part::FaceMakerBullseye
  LengthFwd = 10.6
  LengthRev = 0
  Placement = pos=(0,0,31) rot=(0,0,1;0rad)
  Solid = true
  Symmetric = false
FEATURE [Part::Cylinder] Cylinder023
  Angle = 360
  AttacherType = Attacher::AttachEngine3D
  Height = 20
  Placement = pos=(0,0,36.15) rot=(0,0,1;0rad)
  Radius = 8.2
FEATURE [Part::MultiFuse] Fusion039  label="removeToCreteHoleForPlugHousing008"
  Placement = pos=(-42,19,36) rot=(0,1,0;1.5708rad)
  Shapes = -> [Cylinder023,Cylinder022]
FEATURE [Part::Cut] Cut012
  Base = -> Extrude010
  Placement = pos=(0,0,-0.3) rot=(0,0,1;0rad)
  Tool = -> Fusion039
FEATURE [Part::Cut] Cut013
  Base = -> Box010
  Tool = -> Cut012
FEATURE [Part::Fillet] Fillet014
  Base = -> Cut013
  Edges = 1 edges r=0.7: [Edge13]
FEATURE [Part::Fillet] Fillet015
  Base = -> Fillet014
  Edges = 1 edges r=0.7: [Edge13]
FEATURE [Part::Fillet] Fillet016
  Base = -> Fillet015
  Edges = 1 edges r=0.7: [Edge16]
FEATURE [Part::Fillet] Fillet017
  Base = -> Fillet016
  Edges = 1 edges r=0.7: [Edge11]
FEATURE [Part::Fillet] Fillet018
  Base = -> Fillet017
  Edges = 1 edges r=0.7: [Edge10]
FEATURE [Part::Fillet] Fillet019
  Base = -> Fillet018
  Edges = 1 edges r=1.2: [Edge5]
FEATURE [Part::Fillet] Fillet020
  Base = -> Fillet019
  Edges = 1 edges r=1.2: [Edge12]
FEATURE [Part::Fillet] Fillet021
  Base = -> Fillet020
  Edges = 1 edges r=2: [Edge1]
  Placement = pos=(0.3,0,0) rot=(0,0,1;0rad)
FEATURE [Part::MultiFuse] Fusion040  label="top005"
  Shapes = -> [Cut008,Fillet021]
FEATURE [Part::MultiFuse] Fusion041  label="wireHolder"
  Shapes = -> [Fusion033,Fillet013]
FEATURE [Part::MultiFuse] Fusion042
  Shapes = -> [Fillet007,Fusion041]
FEATURE [Part::MultiFuse] Fusion043  label="wireHolder001"
  Shapes = -> [Fusion042,Fillet010]
FEATURE [Part::MultiFuse] Fusion044  label="wireHolder002"
  Shapes = -> [Fillet006,Fusion037,Fusion043]
FEATURE [Part::Feature] Face026
  shape: bbox 11 x 6 x 2e-07 mm, 1 faces, 0 solids (baked)
FEATURE [Part::Revolution] Revolve026
  Angle = 360
  Axis = (0,1,0)
  Base = (0,0,0)
  FaceMakerClass = Part::FaceMakerBullseye
  Placement = pos=(30.3,-1,19.7) rot=(0,0,1;0rad)
  Solid = false
  Source = -> Face026
  Symmetric = false
FEATURE [Sketcher::SketchObject] Sketch013  label="topSketch006"
  FullyConstrained = true
  sketch-geometry (13):
    g0: LineSegment StartX=117 StartY=19 StartZ=0 EndX=117 EndY=38 EndZ=0
    g1: ArcOfCircle CenterX=98 CenterY=19 CenterZ=0 NormalX=0 NormalY=0 NormalZ=1 AngleXU=0 Radius=19 StartAngle=5.7297 EndAngle=6.28319
    g2: LineSegment StartX=0 StartY=3 StartZ=0 EndX=0 EndY=19 EndZ=0
    g3: LineSegment StartX=19 StartY=38 StartZ=0 EndX=117 EndY=38 EndZ=0
    g4: ArcOfCircle CenterX=19 CenterY=19 CenterZ=0 NormalX=0 NormalY=0 NormalZ=1 AngleXU=0 Radius=19 StartAngle=1.5708 EndAngle=3.14159
    g5: ArcOfCircle CenterX=19 CenterY=19 CenterZ=0 NormalX=0 NormalY=0 NormalZ=1 AngleXU=0 Radius=16 StartAngle=1.5708 EndAngle=3.14159
    g6: ArcOfCircle CenterX=98 CenterY=19 CenterZ=0 NormalX=0 NormalY=0 NormalZ=1 AngleXU=0 Radius=16 StartAngle=5.60905 EndAngle=6.28319
    g7: LineSegment StartX=114 StartY=19 StartZ=0 EndX=114 EndY=35 EndZ=0
    g8: LineSegment StartX=110.5 StartY=9.01251 StartZ=0 EndX=114.163 EndY=9.01251 EndZ=0
    g9: LineSegment StartX=114 StartY=35 StartZ=0 EndX=19 EndY=35 EndZ=0
    g10: LineSegment StartX=0 StartY=3 StartZ=0 EndX=0 EndY=0 EndZ=0
    g11: LineSegment StartX=3 StartY=0 StartZ=0 EndX=0 EndY=0 EndZ=0
    g12: LineSegment StartX=3 StartY=19 StartZ=0 EndX=3 EndY=0 EndZ=0
  constraints (33):
    c: Vertical(g0)
    c: Distance(g0) = 19
    c: Block(g0)
    c: Coincident(g1,g0)
    c: Block(g1)
    c: Vertical(g2)
    c: Block(g2)
    c: Coincident(g3,g0)
    c: Horizontal(g3)
    c: Distance(g3) = 98
    c: Coincident(g4,g3)
    c: Coincident(g4,g2)
    c: Block(g4)
    c: Coincident(g5,g4)
    c: Coincident(g6,g1)
    c: Block(g6)
    c: Block(g5)
    c: Coincident(g7,g6)
    c: Vertical(g7)
    c: Coincident(g8,g6)
    c: Coincident(g8,g1)
    c: Coincident(g9,g7)
    c: Coincident(g9,g5)
    c: Horizontal(g9)
    c: Tangent(g9,g5)
    c: Coincident(g10,g2)
    c: Distance(g10) = 3
    c: Vertical(g10)
    c: Coincident(g11,g10)
    c: Horizontal(g11)
    c: Coincident(g12,g5)
    c: Coincident(g12,g11)
    c: Vertical(g12)
FEATURE [Part::Extrusion] Extrude011  label="top006"
  Base = -> Sketch013
  Dir = (0,0,1)
  DirMode = 2
  FaceMakerClass = Part::FaceMakerBullseye
  LengthFwd = 72
  LengthRev = 0
  Solid = true
  Symmetric = false
FEATURE [Sketcher::SketchObject] Sketch014
  FullyConstrained = true
  MapMode = 3
  Placement = pos=(0,0,0) rot=(1,0,0;1.5708rad)
  Support = -> [Extrude011]
  sketch-geometry (8):
    g0: Circle CenterX=80.351 CenterY=-67.6202 CenterZ=0 NormalX=0 NormalY=0 NormalZ=1 AngleXU=0 Radius=2
    g1: Circle CenterX=80.351 CenterY=-67.6202 CenterZ=0 NormalX=0 NormalY=0 NormalZ=1 AngleXU=0 Radius=3
    g2: Circle CenterX=80.351 CenterY=-4.92017 CenterZ=0 NormalX=0 NormalY=0 NormalZ=1 AngleXU=0 Radius=2
    g3: Circle CenterX=80.351 CenterY=-4.92017 CenterZ=0 NormalX=0 NormalY=0 NormalZ=1 AngleXU=0 Radius=3
    g4: Circle CenterX=23.851 CenterY=-4.92017 CenterZ=0 NormalX=0 NormalY=0 NormalZ=1 AngleXU=0 Radius=2
    g5: Circle CenterX=23.851 CenterY=-4.92017 CenterZ=0 NormalX=0 NormalY=0 NormalZ=1 AngleXU=0 Radius=3
    g6: Circle CenterX=23.851 CenterY=-67.6202 CenterZ=0 NormalX=0 NormalY=0 NormalZ=1 AngleXU=0 Radius=2
    g7: Circle CenterX=23.851 CenterY=-67.6202 CenterZ=0 NormalX=0 NormalY=0 NormalZ=1 AngleXU=0 Radius=3
  constraints (8):
    c: Block(g3)
    c: Block(g2)
    c: Block(g1)
    c: Block(g0)
    c: Block(g6)
    c: Block(g7)
    c: Block(g4)
    c: Block(g5)
FEATURE [Part::Feature] Face027
  shape: bbox 11 x 6 x 2e-07 mm, 1 faces, 0 solids (baked)
FEATURE [Part::Revolution] Revolve027
  Angle = 360
  Axis = (0,1,0)
  Base = (0,0,0)
  FaceMakerClass = Part::FaceMakerBullseye
  Placement = pos=(30.3,-1,51.7) rot=(0,0,1;0rad)
  Solid = false
  Source = -> Face027
  Symmetric = false
FEATURE [Part::Feature] Face028
  shape: bbox 11 x 6 x 2e-07 mm, 1 faces, 0 solids (baked)
FEATURE [Part::Revolution] Revolve028
  Angle = 360
  Axis = (0,1,0)
  Base = (0,0,0)
  FaceMakerClass = Part::FaceMakerBullseye
  Placement = pos=(62.3,-1,19.7) rot=(0,0,1;0rad)
  Solid = false
  Source = -> Face028
  Symmetric = false
FEATURE [Part::Feature] Face029
  shape: bbox 11 x 6 x 2e-07 mm, 1 faces, 0 solids (baked)
FEATURE [Part::Revolution] Revolve029
  Angle = 360
  Axis = (0,1,0)
  Base = (0,0,0)
  FaceMakerClass = Part::FaceMakerBullseye
  Placement = pos=(62.3,-1,51.7) rot=(0,0,1;0rad)
  Solid = false
  Source = -> Face029
  Symmetric = false
FEATURE [Part::Feature] Wire
  shape: bbox 11 x 5.2 x 2e-07 mm, 0 faces, 0 solids (baked)
FEATURE [Part::Revolution] Revolve030
  Angle = 360
  Axis = (0,1,0)
  Base = (0,0,0)
  FaceMakerClass = Part::FaceMakerBullseye
  Placement = pos=(30.3,38,19.7) rot=(0,0,1;0rad)
  Solid = true
  Source = -> Wire
  Symmetric = false
FEATURE [Part::Feature] Wire001
  shape: bbox 11 x 5.2 x 2e-07 mm, 0 faces, 0 solids (baked)
FEATURE [Part::Revolution] Revolve031
  Angle = 360
  Axis = (0,1,0)
  Base = (0,0,0)
  FaceMakerClass = Part::FaceMakerBullseye
  Placement = pos=(30.3,38,51.7) rot=(0,0,1;0rad)
  Solid = true
  Source = -> Wire001
  Symmetric = false
FEATURE [Part::Feature] Wire002
  shape: bbox 11 x 5.2 x 2e-07 mm, 0 faces, 0 solids (baked)
FEATURE [Part::Revolution] Revolve032
  Angle = 360
  Axis = (0,1,0)
  Base = (0,0,0)
  FaceMakerClass = Part::FaceMakerBullseye
  Placement = pos=(62.3,38,51.7) rot=(0,0,1;0rad)
  Solid = true
  Source = -> Wire002
  Symmetric = false
FEATURE [Part::Feature] Wire003
  shape: bbox 11 x 5.2 x 2e-07 mm, 0 faces, 0 solids (baked)
FEATURE [Part::Revolution] Revolve033
  Angle = 360
  Axis = (0,1,0)
  Base = (0,0,0)
  FaceMakerClass = Part::FaceMakerBullseye
  Placement = pos=(62.3,38,19.7) rot=(0,0,1;0rad)
  Solid = true
  Source = -> Wire003
  Symmetric = false
FEATURE [Part::MultiFuse] Fusion045  label="altRandScrewHousing"
  Shapes = -> [Revolve029,Revolve027,Revolve028,Revolve026]
FEATURE [Part::MultiFuse] Fusion046  label="fanScrewHousing"
  Shapes = -> [Revolve033,Revolve032,Revolve031,Revolve030]
FEATURE [Sketcher::SketchObject] Sketch015
  FullyConstrained = true
  sketch-geometry (17):
    g0: Circle CenterX=-3.5 CenterY=23.5 CenterZ=0 NormalX=0 NormalY=0 NormalZ=1 AngleXU=0 Radius=1
    g1: Circle CenterX=-1 CenterY=15.25 CenterZ=0 NormalX=0 NormalY=0 NormalZ=1 AngleXU=0 Radius=1
    g2: Circle CenterX=-3.5 CenterY=7 CenterZ=0 NormalX=0 NormalY=0 NormalZ=1 AngleXU=0 Radius=1
    g3: BSplineCurve PolesCount=3 KnotsCount=2 Degree=2 IsPeriodic=0
    g4: GeomPoint X=-3.5 Y=23.5 Z=0
    g5: GeomPoint X=-3.5 Y=7 Z=0
    g6: Circle CenterX=-4.8 CenterY=30.5 CenterZ=0 NormalX=0 NormalY=0 NormalZ=1 AngleXU=0 Radius=1
    g7: Circle CenterX=-3.5 CenterY=30.5 CenterZ=0 NormalX=0 NormalY=0 NormalZ=1 AngleXU=0 Radius=1
    g8: Circle CenterX=-3.5 CenterY=29.2 CenterZ=0 NormalX=0 NormalY=0 NormalZ=1 AngleXU=0 Radius=1
    g9: BSplineCurve PolesCount=3 KnotsCount=2 Degree=2 IsPeriodic=0
    g10: GeomPoint X=-4.8 Y=30.5 Z=0
    g11: GeomPoint X=-3.5 Y=29.2 Z=0
    g12: LineSegment StartX=-3.5 StartY=29.2 StartZ=0 EndX=-3.5 EndY=23.5 EndZ=0
    g13: LineSegment StartX=-4.8 StartY=30.5 StartZ=0 EndX=0 EndY=30.5 EndZ=0
    g14: LineSegment StartX=-3.5 StartY=0.3 StartZ=0 EndX=0 EndY=0.3 EndZ=0
    g15: LineSegment StartX=-3.5 StartY=0.3 StartZ=0 EndX=-3.5 EndY=7 EndZ=0
    g16: LineSegment StartX=0 StartY=0.3 StartZ=0 EndX=0 EndY=30.5 EndZ=0
  constraints (33):
    c: Weight(g0) = 1
    c: Equal(g0,g1)
    c: Equal(g0,g2)
    c: InternalAlignment(g0,g3)
    c: InternalAlignment(g1,g3)
    c: InternalAlignment(g2,g3)
    c: InternalAlignment(g4,g3)
    c: InternalAlignment(g5,g3)
    c: Block(g3)
    c: Weight(g6) = 1
    c: Equal(g6,g7)
    c: Equal(g6,g8)
    c: InternalAlignment(g6,g9)
    c: InternalAlignment(g7,g9)
    c: InternalAlignment(g8,g9)
    c: InternalAlignment(g10,g9)
    c: InternalAlignment(g11,g9)
    c: Block(g9)
    c: Coincident(g12,g9)
    c: Coincident(g12,g3)
    c: Vertical(g12)
    c: Coincident(g13,g9)
    c: Horizontal(g13)
    c: Distance(g13) = 4.8
    c: Horizontal(g14)
    c: Block(g14)
    c: Coincident(g15,g14)
    c: Coincident(g15,g3)
    c: Vertical(g15)
    c: Coincident(g16,g14)
    c: Coincident(g16,g13)
    c: Vertical(g16)
    c: Tangent(g16,g1)
FEATURE [Sketcher::SketchObject] Sketch016
  FullyConstrained = true
  sketch-geometry (16):
    g0: Circle CenterX=-3.5 CenterY=23.5 CenterZ=0 NormalX=0 NormalY=0 NormalZ=1 AngleXU=0 Radius=1
    g1: Circle CenterX=-1 CenterY=15.25 CenterZ=0 NormalX=0 NormalY=0 NormalZ=1 AngleXU=0 Radius=1
    g2: Circle CenterX=-3.5 CenterY=7 CenterZ=0 NormalX=0 NormalY=0 NormalZ=1 AngleXU=0 Radius=1
    g3: BSplineCurve PolesCount=3 KnotsCount=2 Degree=2 IsPeriodic=0
    g4: GeomPoint X=-3.5 Y=23.5 Z=0
    g5: GeomPoint X=-3.5 Y=7 Z=0
    g6: LineSegment StartX=-3.5 StartY=28.2 StartZ=0 EndX=-3.5 EndY=23.5 EndZ=0
    g7: LineSegment StartX=0 StartY=29.5 StartZ=0 EndX=0 EndY=30 EndZ=0
    g8: LineSegment StartX=-3.5 StartY=28.2 StartZ=0 EndX=-3.5 EndY=30 EndZ=0
    g9: LineSegment StartX=0 StartY=30 StartZ=0 EndX=0 EndY=30.5 EndZ=0
    g10: LineSegment StartX=0 StartY=30.5 StartZ=0 EndX=-3.5 EndY=30.5 EndZ=0
    g11: LineSegment StartX=-3.5 StartY=30.5 StartZ=0 EndX=-3.5 EndY=30 EndZ=0
    g12: LineSegment StartX=0 StartY=29.5 StartZ=0 EndX=0 EndY=5 EndZ=0
    g13: LineSegment StartX=-3.5 StartY=0.3 StartZ=0 EndX=-3.5 EndY=7 EndZ=0
    g14: LineSegment StartX=-3.5 StartY=0.3 StartZ=0 EndX=0 EndY=0.3 EndZ=0
    g15: LineSegment StartX=0 StartY=5 StartZ=0 EndX=0 EndY=0.3 EndZ=0
  constraints (39):
    c: Weight(g0) = 1
    c: Equal(g0,g1)
    c: Equal(g0,g2)
    c: InternalAlignment(g0,g3)
    c: InternalAlignment(g1,g3)
    c: InternalAlignment(g2,g3)
    c: InternalAlignment(g4,g3)
    c: InternalAlignment(g5,g3)
    c: Block(g3)
    c: Coincident(g6,g3)
    c: Vertical(g6)
    c: Vertical(g7)
    c: Distance(g7) = 0.5
    c: Coincident(g8,g6)
    c: Vertical(g8)
    c: Block(g6)
    c: Block(g7)
    c: Vertical(g9)
    c: Equal(g7,g9) = 0.5
    c: Block(g9)
    c: Coincident(g9,g7)
    c: Horizontal(g10)
    c: Coincident(g10,g9)
    c: Coincident(g11,g10)
    c: Coincident(g11,g8)
    c: Vertical(g11)
    c: Block(g11)
    c: Coincident(g12,g7)
    c: Vertical(g12)
    c: Coincident(g13,g3)
    c: Vertical(g13)
    c: Distance(g13) = 6.7
    c: Coincident(g14,g13)
    c: Horizontal(g14)
    c: Block(g14)
    c: Coincident(g15,g12)
    c: Coincident(g15,g14)
    c: Vertical(g15)
    c: Block(g15)
FEATURE [Sketcher::SketchObject] Sketch017
  FullyConstrained = true
  sketch-geometry (11):
    g0: LineSegment StartX=-3.5 StartY=1e-16 StartZ=0 EndX=-1.6 EndY=1e-16 EndZ=0
    g1: LineSegment StartX=-1.6 StartY=1e-16 StartZ=0 EndX=-1.6 EndY=1.5 EndZ=0
    g2: LineSegment StartX=-3.5 StartY=1.5 StartZ=0 EndX=-1.6 EndY=1.5 EndZ=0
    g3: LineSegment StartX=-3.5 StartY=1e-16 StartZ=0 EndX=-4.8 EndY=1e-16 EndZ=0
    g4: Circle CenterX=-3.5 CenterY=1.3 CenterZ=0 NormalX=0 NormalY=0 NormalZ=1 AngleXU=0 Radius=1
    g5: Circle CenterX=-3.5 CenterY=1e-16 CenterZ=0 NormalX=0 NormalY=0 NormalZ=1 AngleXU=0 Radius=1
    g6: Circle CenterX=-4.8 CenterY=1e-16 CenterZ=0 NormalX=0 NormalY=0 NormalZ=1 AngleXU=0 Radius=1
    g7: BSplineCurve PolesCount=3 KnotsCount=2 Degree=2 IsPeriodic=0
    g8: GeomPoint X=-3.5 Y=1.3 Z=0
    g9: GeomPoint X=-4.8 Y=1e-16 Z=0
    g10: LineSegment StartX=-3.5 StartY=1.3 StartZ=0 EndX=-3.5 EndY=1.5 EndZ=0
  constraints (24):
    c: Horizontal(g0)
    c: Distance(g0) = 1.9
    c: Block(g0)
    c: Coincident(g1,g0)
    c: Vertical(g1)
    c: Coincident(g2,g1)
    c: Horizontal(g2)
    c: Coincident(g3,g0)
    c: Horizontal(g3)
    c: Distance(g3) = 1.3
    c: Weight(g4) = 1
    c: Equal(g4,g5)
    c: Coincident(g5,g0)
    c: Equal(g4,g6)
    c: Coincident(g7,g3)
    c: InternalAlignment(g4,g7)
    c: InternalAlignment(g5,g7)
    c: InternalAlignment(g6,g7)
    c: InternalAlignment(g8,g7)
    c: InternalAlignment(g9,g7)
    c: Coincident(g10,g7)
    c: Coincident(g10,g2)
    c: Vertical(g10)
    c: Block(g10)
FEATURE [Part::Feature] Face035
  shape: bbox 3.2 x 1.5 x 2e-07 mm, 1 faces, 0 solids (baked)
FEATURE [Part::Revolution] Revolve039  label="backCaseScrewRetainer"
  Angle = 360
  Axis = (0,1,0)
  Base = (0,0,0)
  FaceMakerClass = Part::FaceMakerBullseye
  Placement = pos=(12.5,3,62) rot=(0,0,1;0rad)
  Solid = false
  Source = -> Face035
  Symmetric = false
FEATURE [Part::Feature] Face036
  shape: bbox 3.2 x 1.5 x 2e-07 mm, 1 faces, 0 solids (baked)
FEATURE [Part::Feature] Face039
  shape: bbox 4.8 x 30.2 x 2e-07 mm, 1 faces, 0 solids (baked)
FEATURE [Part::Revolution] Revolve043  label="frontCaseScrewPost002"
  Angle = 360
  Axis = (0,1,0)
  Base = (0,0,0)
  FaceMakerClass = Part::FaceMakerBullseye
  Placement = pos=(89.5,4.5,3.5) rot=(0,0,1;0rad)
  Solid = false
  Source = -> Face039
  Symmetric = false
FEATURE [Part::Feature] Face042
  shape: bbox 4.8 x 30.2 x 2e-07 mm, 1 faces, 0 solids (baked)
FEATURE [Part::Revolution] Revolve046  label="frontCaseScrewPost003"
  Angle = 360
  Axis = (0,1,0)
  Base = (0,0,0)
  FaceMakerClass = Part::FaceMakerBullseye
  Placement = pos=(89.5,4.5,68.5) rot=(0,0,1;0rad)
  Solid = false
  Source = -> Face042
  Symmetric = false
FEATURE [Part::Feature] Face043
  shape: bbox 3.2 x 1.5 x 2e-07 mm, 1 faces, 0 solids (baked)
FEATURE [Part::Revolution] Revolve047  label="frontCaseScrewRetainer002"
  Angle = 360
  Axis = (0,1,0)
  Base = (0,0,0)
  FaceMakerClass = Part::FaceMakerBullseye
  Placement = pos=(89.5,3,68.5) rot=(0,0,1;0rad)
  Solid = false
  Source = -> Face043
  Symmetric = false
FEATURE [Part::Feature] Face044
  shape: bbox 3.2 x 1.5 x 2e-07 mm, 1 faces, 0 solids (baked)
FEATURE [Part::Revolution] Revolve048  label="frontCaseScrewRetainer003"
  Angle = 360
  Axis = (0,1,0)
  Base = (0,0,0)
  FaceMakerClass = Part::FaceMakerBullseye
  Placement = pos=(89.5,3,3.5) rot=(0,0,1;0rad)
  Solid = false
  Source = -> Face044
  Symmetric = false
FEATURE [App::MeasureDistance] Distance002  label="Distance: 1.67 mm"
  Distance = 1.66921
  P1 = (99.2361,4.7524,71.7)
  P2 = (99.2347,6.42161,71.7)
FEATURE [Sketcher::SketchObject] Sketch018
  FullyConstrained = true
  sketch-geometry (7):
    g0: LineSegment StartX=0 StartY=0 StartZ=0 EndX=0 EndY=6 EndZ=0
    g1: Circle CenterX=0 CenterY=0 CenterZ=0 NormalX=0 NormalY=0 NormalZ=1 AngleXU=0 Radius=1
    g2: Circle CenterX=8 CenterY=6 CenterZ=0 NormalX=0 NormalY=0 NormalZ=1 AngleXU=0 Radius=1
    g3: BSplineCurve PolesCount=3 KnotsCount=2 Degree=2 IsPeriodic=0
    g4: GeomPoint X=0 Y=0 Z=0
    g5: GeomPoint X=8 Y=6 Z=0
    g6: LineSegment StartX=0 StartY=6 StartZ=0 EndX=8 EndY=6 EndZ=0
  constraints (14):
    c: Coincident(g0,g-1)
    c: Distance(g0) = 6
    c: Vertical(g0)
    c: Coincident(g3,g0)
    c: Weight(g1) = 1
    c: Equal(g1,g2)
    c: InternalAlignment(g1,g3)
    c: InternalAlignment(g2,g3)
    c: InternalAlignment(g4,g3)
    c: InternalAlignment(g5,g3)
    c: Block(g3)
    c: Coincident(g6,g0)
    c: Coincident(g6,g3)
    c: Horizontal(g6)
FEATURE [Part::Extrusion] Extrude012  label="caseScrewPillarBracket"
  Base = -> Sketch018
  Dir = (0,0,1)
  DirMode = 2
  FaceMakerClass = Part::FaceMakerBullseye
  LengthFwd = 2.4
  LengthRev = 0
  Placement = pos=(15.76,29,8.8) rot=(0,1,0;0rad)
  Solid = true
  Symmetric = false
FEATURE [Sketcher::SketchObject] Sketch019
  FullyConstrained = true
  sketch-geometry (7):
    g0: LineSegment StartX=0 StartY=0 StartZ=0 EndX=0 EndY=6 EndZ=0
    g1: Circle CenterX=0 CenterY=0 CenterZ=0 NormalX=0 NormalY=0 NormalZ=1 AngleXU=0 Radius=1
    g2: Circle CenterX=8 CenterY=6 CenterZ=0 NormalX=0 NormalY=0 NormalZ=1 AngleXU=0 Radius=1
    g3: BSplineCurve PolesCount=3 KnotsCount=2 Degree=2 IsPeriodic=0
    g4: GeomPoint X=0 Y=0 Z=0
    g5: GeomPoint X=8 Y=6 Z=0
    g6: LineSegment StartX=0 StartY=6 StartZ=0 EndX=8 EndY=6 EndZ=0
  constraints (14):
    c: Coincident(g0,g-1)
    c: Distance(g0) = 6
    c: Vertical(g0)
    c: Coincident(g3,g0)
    c: Weight(g1) = 1
    c: Equal(g1,g2)
    c: InternalAlignment(g1,g3)
    c: InternalAlignment(g2,g3)
    c: InternalAlignment(g4,g3)
    c: InternalAlignment(g5,g3)
    c: Block(g3)
    c: Coincident(g6,g0)
    c: Coincident(g6,g3)
    c: Horizontal(g6)
FEATURE [Part::Extrusion] Extrude013  label="caseScrewPillarBracket001"
  Base = -> Sketch019
  Dir = (0,0,1)
  DirMode = 2
  FaceMakerClass = Part::FaceMakerBullseye
  LengthFwd = 2.4
  LengthRev = 0
  Placement = pos=(15.76,29,60.8) rot=(0,0,1;0rad)
  Solid = true
  Symmetric = false
FEATURE [Sketcher::SketchObject] Sketch020
  FullyConstrained = true
  sketch-geometry (7):
    g0: LineSegment StartX=0 StartY=0 StartZ=0 EndX=0 EndY=6 EndZ=0
    g1: Circle CenterX=0 CenterY=0 CenterZ=0 NormalX=0 NormalY=0 NormalZ=1 AngleXU=0 Radius=1
    g2: Circle CenterX=8 CenterY=6 CenterZ=0 NormalX=0 NormalY=0 NormalZ=1 AngleXU=0 Radius=1
    g3: BSplineCurve PolesCount=3 KnotsCount=2 Degree=2 IsPeriodic=0
    g4: GeomPoint X=0 Y=0 Z=0
    g5: GeomPoint X=8 Y=6 Z=0
    g6: LineSegment StartX=0 StartY=6 StartZ=0 EndX=8 EndY=6 EndZ=0
  constraints (14):
    c: Coincident(g0,g-1)
    c: Distance(g0) = 6
    c: Vertical(g0)
    c: Coincident(g3,g0)
    c: Weight(g1) = 1
    c: Equal(g1,g2)
    c: InternalAlignment(g1,g3)
    c: InternalAlignment(g2,g3)
    c: InternalAlignment(g4,g3)
    c: InternalAlignment(g5,g3)
    c: Block(g3)
    c: Coincident(g6,g0)
    c: Coincident(g6,g3)
    c: Horizontal(g6)
FEATURE [Part::Extrusion] Extrude014  label="caseScrewPillarBracket002"
  Base = -> Sketch020
  Dir = (0,0,1)
  DirMode = 2
  FaceMakerClass = Part::FaceMakerBullseye
  LengthFwd = 2.4
  LengthRev = 0
  Placement = pos=(13.7,29,13.26) rot=(0,1,0;-1.5708rad)
  Solid = true
  Symmetric = false
FEATURE [Sketcher::SketchObject] Sketch021
  FullyConstrained = true
  sketch-geometry (7):
    g0: LineSegment StartX=0 StartY=0 StartZ=0 EndX=0 EndY=6 EndZ=0
    g1: Circle CenterX=0 CenterY=0 CenterZ=0 NormalX=0 NormalY=0 NormalZ=1 AngleXU=0 Radius=1
    g2: Circle CenterX=8 CenterY=6 CenterZ=0 NormalX=0 NormalY=0 NormalZ=1 AngleXU=0 Radius=1
    g3: BSplineCurve PolesCount=3 KnotsCount=2 Degree=2 IsPeriodic=0
    g4: GeomPoint X=0 Y=0 Z=0
    g5: GeomPoint X=8 Y=6 Z=0
    g6: LineSegment StartX=0 StartY=6 StartZ=0 EndX=8 EndY=6 EndZ=0
  constraints (14):
    c: Coincident(g0,g-1)
    c: Distance(g0) = 6
    c: Vertical(g0)
    c: Coincident(g3,g0)
    c: Weight(g1) = 1
    c: Equal(g1,g2)
    c: InternalAlignment(g1,g3)
    c: InternalAlignment(g2,g3)
    c: InternalAlignment(g4,g3)
    c: InternalAlignment(g5,g3)
    c: Block(g3)
    c: Coincident(g6,g0)
    c: Coincident(g6,g3)
    c: Horizontal(g6)
FEATURE [Part::Extrusion] Extrude015  label="caseScrewPillarBracket003"
  Base = -> Sketch021
  Dir = (0,0,1)
  DirMode = 2
  FaceMakerClass = Part::FaceMakerBullseye
  LengthFwd = 2.4
  LengthRev = 0
  Placement = pos=(11.3,29,58.74) rot=(0,1,0;1.5708rad)
  Solid = true
  Symmetric = false
FEATURE [Sketcher::SketchObject] Sketch022
  FullyConstrained = true
  sketch-geometry (7):
    g0: LineSegment StartX=0 StartY=0 StartZ=0 EndX=0 EndY=6 EndZ=0
    g1: Circle CenterX=0 CenterY=0 CenterZ=0 NormalX=0 NormalY=0 NormalZ=1 AngleXU=0 Radius=1
    g2: Circle CenterX=8 CenterY=6 CenterZ=0 NormalX=0 NormalY=0 NormalZ=1 AngleXU=0 Radius=1
    g3: BSplineCurve PolesCount=3 KnotsCount=2 Degree=2 IsPeriodic=0
    g4: GeomPoint X=0 Y=0 Z=0
    g5: GeomPoint X=8 Y=6 Z=0
    g6: LineSegment StartX=0 StartY=6 StartZ=0 EndX=8 EndY=6 EndZ=0
  constraints (14):
    c: Coincident(g0,g-1)
    c: Distance(g0) = 6
    c: Vertical(g0)
    c: Coincident(g3,g0)
    c: Weight(g1) = 1
    c: Equal(g1,g2)
    c: InternalAlignment(g1,g3)
    c: InternalAlignment(g2,g3)
    c: InternalAlignment(g4,g3)
    c: InternalAlignment(g5,g3)
    c: Block(g3)
    c: Coincident(g6,g0)
    c: Coincident(g6,g3)
    c: Horizontal(g6)
FEATURE [Part::Extrusion] Extrude016  label="caseScrewPillarBracket004"
  Base = -> Sketch022
  Dir = (0,0,1)
  DirMode = 2
  FaceMakerClass = Part::FaceMakerBullseye
  LengthFwd = 2.4
  LengthRev = 0
  Placement = pos=(88.3,29,65.23) rot=(0,1,0;1.5708rad)
  Solid = true
  Symmetric = false
FEATURE [Sketcher::SketchObject] Sketch023
  FullyConstrained = true
  sketch-geometry (7):
    g0: LineSegment StartX=0 StartY=0 StartZ=0 EndX=0 EndY=6 EndZ=0
    g1: Circle CenterX=0 CenterY=0 CenterZ=0 NormalX=0 NormalY=0 NormalZ=1 AngleXU=0 Radius=1
    g2: Circle CenterX=8 CenterY=6 CenterZ=0 NormalX=0 NormalY=0 NormalZ=1 AngleXU=0 Radius=1
    g3: BSplineCurve PolesCount=3 KnotsCount=2 Degree=2 IsPeriodic=0
    g4: GeomPoint X=0 Y=0 Z=0
    g5: GeomPoint X=8 Y=6 Z=0
    g6: LineSegment StartX=0 StartY=6 StartZ=0 EndX=8 EndY=6 EndZ=0
  constraints (14):
    c: Coincident(g0,g-1)
    c: Distance(g0) = 6
    c: Vertical(g0)
    c: Coincident(g3,g0)
    c: Weight(g1) = 1
    c: Equal(g1,g2)
    c: InternalAlignment(g1,g3)
    c: InternalAlignment(g2,g3)
    c: InternalAlignment(g4,g3)
    c: InternalAlignment(g5,g3)
    c: Block(g3)
    c: Coincident(g6,g0)
    c: Coincident(g6,g3)
    c: Horizontal(g6)
FEATURE [Part::Extrusion] Extrude017  label="caseScrewPillarBracket005"
  Base = -> Sketch023
  Dir = (0,0,1)
  DirMode = 2
  FaceMakerClass = Part::FaceMakerBullseye
  LengthFwd = 2.4
  LengthRev = 0
  Placement = pos=(90.7,29,6.77) rot=(0,-1,0;1.5708rad)
  Solid = true
  Symmetric = false
FEATURE [Sketcher::SketchObject] Sketch024
  FullyConstrained = true
  sketch-geometry (7):
    g0: LineSegment StartX=0 StartY=0 StartZ=0 EndX=0 EndY=6 EndZ=0
    g1: Circle CenterX=0 CenterY=0 CenterZ=0 NormalX=0 NormalY=0 NormalZ=1 AngleXU=0 Radius=1
    g2: Circle CenterX=8 CenterY=6 CenterZ=0 NormalX=0 NormalY=0 NormalZ=1 AngleXU=0 Radius=1
    g3: BSplineCurve PolesCount=3 KnotsCount=2 Degree=2 IsPeriodic=0
    g4: GeomPoint X=0 Y=0 Z=0
    g5: GeomPoint X=8 Y=6 Z=0
    g6: LineSegment StartX=0 StartY=6 StartZ=0 EndX=8 EndY=6 EndZ=0
  constraints (14):
    c: Coincident(g0,g-1)
    c: Distance(g0) = 6
    c: Vertical(g0)
    c: Coincident(g3,g0)
    c: Weight(g1) = 1
    c: Equal(g1,g2)
    c: InternalAlignment(g1,g3)
    c: InternalAlignment(g2,g3)
    c: InternalAlignment(g4,g3)
    c: InternalAlignment(g5,g3)
    c: Block(g3)
    c: Coincident(g6,g0)
    c: Coincident(g6,g3)
    c: Horizontal(g6)
FEATURE [Part::Extrusion] Extrude018  label="caseScrewPillarBracket006"
  Base = -> Sketch024
  Dir = (0,0,1)
  DirMode = 2
  FaceMakerClass = Part::FaceMakerBullseye
  LengthFwd = 2.4
  LengthRev = 0
  Placement = pos=(103.7,29,6.77) rot=(0,-1,0;1.5708rad)
  Solid = true
  Symmetric = false
FEATURE [Sketcher::SketchObject] Sketch025
  FullyConstrained = true
  sketch-geometry (7):
    g0: LineSegment StartX=0 StartY=0 StartZ=0 EndX=0 EndY=6 EndZ=0
    g1: Circle CenterX=0 CenterY=0 CenterZ=0 NormalX=0 NormalY=0 NormalZ=1 AngleXU=0 Radius=1
    g2: Circle CenterX=8 CenterY=6 CenterZ=0 NormalX=0 NormalY=0 NormalZ=1 AngleXU=0 Radius=1
    g3: BSplineCurve PolesCount=3 KnotsCount=2 Degree=2 IsPeriodic=0
    g4: GeomPoint X=0 Y=0 Z=0
    g5: GeomPoint X=8 Y=6 Z=0
    g6: LineSegment StartX=0 StartY=6 StartZ=0 EndX=8 EndY=6 EndZ=0
  constraints (14):
    c: Coincident(g0,g-1)
    c: Distance(g0) = 6
    c: Vertical(g0)
    c: Coincident(g3,g0)
    c: Weight(g1) = 1
    c: Equal(g1,g2)
    c: InternalAlignment(g1,g3)
    c: InternalAlignment(g2,g3)
    c: InternalAlignment(g4,g3)
    c: InternalAlignment(g5,g3)
    c: Block(g3)
    c: Coincident(g6,g0)
    c: Coincident(g6,g3)
    c: Horizontal(g6)
FEATURE [Part::Extrusion] Extrude019  label="caseScrewPillarBracket007"
  Base = -> Sketch025
  Dir = (0,0,1)
  DirMode = 2
  FaceMakerClass = Part::FaceMakerBullseye
  LengthFwd = 2.4
  LengthRev = 0
  Placement = pos=(101.3,29,65.23) rot=(0,1,0;1.5708rad)
  Solid = true
  Symmetric = false
FEATURE [Part::Box] Box011  label="frontCaseScrewPillarBracket"
  AttacherType = Attacher::AttachEngine3D
  Height = 2.4
  Length = 16
  Placement = pos=(87,28,2.3) rot=(0,0,1;0rad)
  Width = 7
FEATURE [Part::Box] Box012  label="frontCaseScrewPillarBracket001"
  AttacherType = Attacher::AttachEngine3D
  Height = 2.4
  Length = 16
  Placement = pos=(87,28,67.3) rot=(0,0,1;0rad)
  Width = 7
FEATURE [Sketcher::SketchObject] Sketch026
  FullyConstrained = true
  sketch-geometry (17):
    g0: Circle CenterX=-3.5 CenterY=23.5 CenterZ=0 NormalX=0 NormalY=0 NormalZ=1 AngleXU=0 Radius=1
    g1: Circle CenterX=-1 CenterY=15.25 CenterZ=0 NormalX=0 NormalY=0 NormalZ=1 AngleXU=0 Radius=1
    g2: Circle CenterX=-3.5 CenterY=7 CenterZ=0 NormalX=0 NormalY=0 NormalZ=1 AngleXU=0 Radius=1
    g3: BSplineCurve PolesCount=3 KnotsCount=2 Degree=2 IsPeriodic=0
    g4: GeomPoint X=-3.5 Y=23.5 Z=0
    g5: GeomPoint X=-3.5 Y=7 Z=0
    g6: Circle CenterX=-4.8 CenterY=30.5 CenterZ=0 NormalX=0 NormalY=0 NormalZ=1 AngleXU=0 Radius=1
    g7: Circle CenterX=-3.5 CenterY=30.5 CenterZ=0 NormalX=0 NormalY=0 NormalZ=1 AngleXU=0 Radius=1
    g8: Circle CenterX=-3.5 CenterY=29.2 CenterZ=0 NormalX=0 NormalY=0 NormalZ=1 AngleXU=0 Radius=1
    g9: BSplineCurve PolesCount=3 KnotsCount=2 Degree=2 IsPeriodic=0
    g10: GeomPoint X=-4.8 Y=30.5 Z=0
    g11: GeomPoint X=-3.5 Y=29.2 Z=0
    g12: LineSegment StartX=-3.5 StartY=29.2 StartZ=0 EndX=-3.5 EndY=23.5 EndZ=0
    g13: LineSegment StartX=-4.8 StartY=30.5 StartZ=0 EndX=0 EndY=30.5 EndZ=0
    g14: LineSegment StartX=-3.5 StartY=5 StartZ=0 EndX=-3.5 EndY=7 EndZ=0
    g15: LineSegment StartX=0 StartY=5 StartZ=0 EndX=0 EndY=30.5 EndZ=0
    g16: LineSegment StartX=-3.5 StartY=5 StartZ=0 EndX=0 EndY=5 EndZ=0
  constraints (33):
    c: Weight(g0) = 1
    c: Equal(g0,g1)
    c: Equal(g0,g2)
    c: InternalAlignment(g0,g3)
    c: InternalAlignment(g1,g3)
    c: InternalAlignment(g2,g3)
    c: InternalAlignment(g4,g3)
    c: InternalAlignment(g5,g3)
    c: Block(g3)
    c: Weight(g6) = 1
    c: Equal(g6,g7)
    c: Equal(g6,g8)
    c: InternalAlignment(g6,g9)
    c: InternalAlignment(g7,g9)
    c: InternalAlignment(g8,g9)
    c: InternalAlignment(g10,g9)
    c: InternalAlignment(g11,g9)
    c: Block(g9)
    c: Coincident(g12,g9)
    c: Coincident(g12,g3)
    c: Vertical(g12)
    c: Coincident(g13,g9)
    c: Horizontal(g13)
    c: Distance(g13) = 4.8
    c: Coincident(g14,g3)
    c: Vertical(g14)
    c: Coincident(g15,g13)
    c: Vertical(g15)
    c: Tangent(g15,g1)
    c: Distance(g14) = 2
    c: Coincident(g16,g14)
    c: Horizontal(g16)
    c: Coincident(g15,g16)
FEATURE [Part::Feature] Face050
  shape: bbox 4.8 x 25.5 x 2e-07 mm, 1 faces, 0 solids (baked)
FEATURE [Part::Revolution] Revolve054  label="moreFrontCaseScrewPost001"
  Angle = 360
  Axis = (0,1,0)
  Base = (0,0,0)
  FaceMakerClass = Part::FaceMakerBullseye
  Placement = pos=(102.5,4.5,3.5) rot=(0,0,1;0rad)
  Solid = false
  Source = -> Face050
  Symmetric = false
FEATURE [Part::Feature] Face051
  shape: bbox 4.8 x 25.5 x 2e-07 mm, 1 faces, 0 solids (baked)
FEATURE [Part::Revolution] Revolve055  label="moreFrontCaseScrewPost002"
  Angle = 360
  Axis = (0,1,0)
  Base = (0,0,0)
  FaceMakerClass = Part::FaceMakerBullseye
  Placement = pos=(102.5,4.5,68.5) rot=(0,0,1;0rad)
  Solid = false
  Source = -> Face051
  Symmetric = false
FEATURE [Sketcher::SketchObject] Sketch027
  FullyConstrained = true
  sketch-geometry (10):
    g0: LineSegment StartX=-1.6 StartY=4.7 StartZ=0 EndX=-1.6 EndY=1.7 EndZ=0
    g1: LineSegment StartX=-3.5 StartY=4.7 StartZ=0 EndX=-1.6 EndY=4.7 EndZ=0
    g2: LineSegment StartX=-1.6 StartY=1.7 StartZ=0 EndX=-1.6 EndY=1.5 EndZ=0
    g3: LineSegment StartX=-1.6 StartY=1.5 StartZ=0 EndX=-5.2 EndY=1.5 EndZ=0
    g4: Circle CenterX=-3.5 CenterY=4.7 CenterZ=0 NormalX=0 NormalY=0 NormalZ=1 AngleXU=0 Radius=1
    g5: Circle CenterX=-3.59627 CenterY=2.99743 CenterZ=0 NormalX=0 NormalY=0 NormalZ=1 AngleXU=0 Radius=1
    g6: Circle CenterX=-5.2 CenterY=1.5 CenterZ=0 NormalX=0 NormalY=0 NormalZ=1 AngleXU=0 Radius=1
    g7: BSplineCurve PolesCount=3 KnotsCount=2 Degree=2 IsPeriodic=0
    g8: GeomPoint X=-3.5 Y=4.7 Z=0
    g9: GeomPoint X=-5.2 Y=1.5 Z=0
  constraints (23):
    c: Vertical(g0)
    c: Distance(g0) = 3
    c: Coincident(g1,g0)
    c: Horizontal(g1)
    c: Block(g0)
    c: Block(g1)
    c: Coincident(g2,g0)
    c: Vertical(g2)
    c: Distance(g2) = 0.2
    c: Coincident(g3,g2)
    c: Horizontal(g3)
    c: Block(g3)
    c: Coincident(g7,g1)
    c: Weight(g4) = 1
    c: Equal(g4,g5)
    c: Equal(g4,g6)
    c: Coincident(g7,g3)
    c: InternalAlignment(g4,g7)
    c: InternalAlignment(g5,g7)
    c: InternalAlignment(g6,g7)
    c: InternalAlignment(g8,g7)
    c: InternalAlignment(g9,g7)
    c: Block(g7)
FEATURE [Sketcher::SketchObject] Sketch028
  FullyConstrained = true
  sketch-geometry (18):
    g0: LineSegment StartX=0 StartY=3e-16 StartZ=0 EndX=0 EndY=1.7 EndZ=0
    g1: LineSegment StartX=-3.5 StartY=0 StartZ=0 EndX=-3.5 EndY=0.9 EndZ=0
    g2: Circle CenterX=-2.7 CenterY=1.7 CenterZ=0 NormalX=0 NormalY=0 NormalZ=1 AngleXU=0 Radius=1
    g3: Circle CenterX=-3.5 CenterY=1.7 CenterZ=0 NormalX=0 NormalY=0 NormalZ=1 AngleXU=0 Radius=1
    g4: Circle CenterX=-3.5 CenterY=0.9 CenterZ=0 NormalX=0 NormalY=0 NormalZ=1 AngleXU=0 Radius=1
    g5: BSplineCurve PolesCount=3 KnotsCount=2 Degree=2 IsPeriodic=0
    g6: GeomPoint X=-2.7 Y=1.7 Z=0
    g7: GeomPoint X=-3.5 Y=0.9 Z=0
    g8: LineSegment StartX=-3.5 StartY=0 StartZ=0 EndX=-3.5 EndY=-7 EndZ=0
    g9: LineSegment StartX=0 StartY=3e-16 StartZ=0 EndX=0 EndY=-7 EndZ=0
    g10: LineSegment StartX=-3.5 StartY=-7 StartZ=0 EndX=0 EndY=-7 EndZ=0
    g11: LineSegment StartX=-2.7 StartY=1.7 StartZ=0 EndX=-1.6 EndY=1.7 EndZ=0
    g12: LineSegment StartX=0 StartY=1.7 StartZ=0 EndX=0 EndY=4.5 EndZ=0
    g13: LineSegment StartX=0 StartY=4.5 StartZ=0 EndX=0 EndY=10.8 EndZ=0
    g14: LineSegment StartX=0 StartY=10.8 StartZ=0 EndX=-2 EndY=10.8 EndZ=0
    g15: LineSegment StartX=-1.6 StartY=4.7 StartZ=0 EndX=-1.6 EndY=1.7 EndZ=0
    g16: LineSegment StartX=-1.6 StartY=4.7 StartZ=0 EndX=-2 EndY=4.7 EndZ=0
    g17: LineSegment StartX=-2 StartY=4.7 StartZ=0 EndX=-2 EndY=10.8 EndZ=0
  constraints (44):
    c: Vertical(g0)
    c: Vertical(g1)
    c: Distance(g1) = 0.9
    c: Block(g0)
    c: Distance(g0) = 1.7
    c: Weight(g2) = 1
    c: Equal(g2,g3)
    c: Equal(g2,g4)
    c: Coincident(g5,g1)
    c: InternalAlignment(g2,g5)
    c: InternalAlignment(g3,g5)
    c: InternalAlignment(g4,g5)
    c: InternalAlignment(g6,g5)
    c: InternalAlignment(g7,g5)
    c: Block(g5)
    c: Coincident(g8,g1)
    c: Vertical(g8)
    c: Distance(g8) = 7
    c: Vertical(g9)
    c: Equal(g8,g9) = 7
    c: Coincident(g9,g0)
    c: Coincident(g10,g8)
    c: Coincident(g10,g9)
    c: Horizontal(g10)
    c: Coincident(g11,g5)
    c: Horizontal(g11)
    c: Coincident(g12,g0)
    c: Vertical(g12)
    c: Distance(g12) = 2.8
    c: Coincident(g13,g12)
    c: Vertical(g13)
    c: Distance(g13) = 6.3
    c: Coincident(g14,g13)
    c: Horizontal(g14)
    c: Distance(g14) = 2
    c: Vertical(g15)
    c: Distance(g15) = 3
    c: Block(g11)
    c: Coincident(g15,g11)
    c: Coincident(g16,g15)
    c: Horizontal(g16)
    c: Coincident(g17,g16)
    c: Coincident(g17,g14)
    c: Vertical(g17)
FEATURE [Part::Revolution] Revolve040  label="backCaseScrewRetainer001"
  Angle = 360
  Axis = (0,1,0)
  Base = (0,0,0)
  FaceMakerClass = Part::FaceMakerBullseye
  Placement = pos=(12.5,3,10) rot=(0,0,1;0rad)
  Solid = false
  Source = -> Face036
  Symmetric = false
FEATURE [Part::Feature] Face055
  shape: bbox 3.5 x 30.2 x 2e-07 mm, 1 faces, 0 solids (baked)
FEATURE [Part::Revolution] Revolve059  label="backCaseScrewPost"
  Angle = 360
  Axis = (0,1,0)
  Base = (0,0,0)
  FaceMakerClass = Part::FaceMakerBullseye
  Placement = pos=(12.5,4.5,10) rot=(0,0,1;0rad)
  Solid = false
  Source = -> Face055
  Symmetric = false
FEATURE [Part::Feature] Face056
  shape: bbox 3.5 x 30.2 x 2e-07 mm, 1 faces, 0 solids (baked)
FEATURE [Part::Revolution] Revolve060  label="backCaseScrewPost001"
  Angle = 360
  Axis = (0,1,0)
  Base = (0,0,0)
  FaceMakerClass = Part::FaceMakerBullseye
  Placement = pos=(12.5,4.5,62) rot=(0,0,1;0rad)
  Solid = false
  Source = -> Face056
  Symmetric = false
FEATURE [Part::Feature] Face057
  shape: bbox 3.5 x 17.8 x 2e-07 mm, 1 faces, 0 solids (baked)
FEATURE [Part::Revolution] Revolve061  label="removeToCreateScrewAndThreadedInsertHole"
  Angle = 360
  Axis = (0,1,0)
  Base = (0,0,0)
  FaceMakerClass = Part::FaceMakerBullseye
  Placement = pos=(12.5,0,10) rot=(0,0,1;0rad)
  Solid = false
  Source = -> Face057
  Symmetric = false
FEATURE [Part::Feature] Face058
  shape: bbox 3.5 x 17.8 x 2e-07 mm, 1 faces, 0 solids (baked)
FEATURE [Part::Revolution] Revolve062  label="removeToCreateScrewAndThreadedInsertHole001"
  Angle = 360
  Axis = (0,1,0)
  Base = (0,0,0)
  FaceMakerClass = Part::FaceMakerBullseye
  Placement = pos=(12.5,0,62) rot=(0,0,1;0rad)
  Solid = false
  Source = -> Face058
  Symmetric = false
FEATURE [Part::Feature] Face059
  shape: bbox 3.5 x 17.8 x 2e-07 mm, 1 faces, 0 solids (baked)
FEATURE [Part::Revolution] Revolve063  label="removeToCreateScrewAndThreadedInsertHole002"
  Angle = 360
  Axis = (0,1,0)
  Base = (0,0,0)
  FaceMakerClass = Part::FaceMakerBullseye
  Placement = pos=(89.5,0,68.5) rot=(0,0,1;0rad)
  Solid = false
  Source = -> Face059
  Symmetric = false
FEATURE [Part::Feature] Face060
  shape: bbox 3.5 x 17.8 x 2e-07 mm, 1 faces, 0 solids (baked)
FEATURE [Part::Revolution] Revolve064  label="removeToCreateScrewAndThreadedInsertHole003"
  Angle = 360
  Axis = (0,1,0)
  Base = (0,0,0)
  FaceMakerClass = Part::FaceMakerBullseye
  Placement = pos=(89.5,0,3.5) rot=(0,0,1;0rad)
  Solid = false
  Source = -> Face060
  Symmetric = false
FEATURE [Part::Feature] Face061
  shape: bbox 3.5 x 17.8 x 2e-07 mm, 1 faces, 0 solids (baked)
FEATURE [Part::Revolution] Revolve065  label="removeToCreateScrewAndThreadedInsertHole004"
  Angle = 360
  Axis = (0,1,0)
  Base = (0,0,0)
  FaceMakerClass = Part::FaceMakerBullseye
  Placement = pos=(102.5,4.7,3.5) rot=(0,0,1;0rad)
  Solid = false
  Source = -> Face061
  Symmetric = false
FEATURE [Part::Feature] Face062
  shape: bbox 3.5 x 17.8 x 2e-07 mm, 1 faces, 0 solids (baked)
FEATURE [Part::Revolution] Revolve066  label="removeToCreateScrewAndThreadedInsertHole005"
  Angle = 360
  Axis = (0,1,0)
  Base = (0,0,0)
  FaceMakerClass = Part::FaceMakerBullseye
  Placement = pos=(102.5,4.7,68.5) rot=(0,0,1;0rad)
  Solid = false
  Source = -> Face062
  Symmetric = false
FEATURE [Part::MultiFuse] Fusion047  label="makeHoles"
  Shapes = -> [Revolve066,Revolve065,Revolve064,Revolve063,Revolve062,Revolve061]
FEATURE [Part::Feature] Face063
  shape: bbox 3.6 x 3.2 x 2e-07 mm, 1 faces, 0 solids (baked)
FEATURE [Part::Revolution] Revolve067  label="moreFrontCaseScrewRetainer002"
  Angle = 360
  Axis = (0,1,0)
  Base = (0,0,0)
  FaceMakerClass = Part::FaceMakerBullseye
  Placement = pos=(102.5,4.5,68.5) rot=(0,0,1;0rad)
  Solid = false
  Source = -> Face063
  Symmetric = false
FEATURE [Part::Feature] Face064
  shape: bbox 3.6 x 3.2 x 2e-07 mm, 1 faces, 0 solids (baked)
FEATURE [Part::Revolution] Revolve068  label="moreFrontCaseScrewRetainer003"
  Angle = 360
  Axis = (0,1,0)
  Base = (0,0,0)
  FaceMakerClass = Part::FaceMakerBullseye
  Placement = pos=(102.5,4.5,3.5) rot=(0,0,1;0rad)
  Solid = false
  Source = -> Face064
  Symmetric = false
FEATURE [Part::Feature] Face065
  shape: bbox 3.5 x 17.8 x 2e-07 mm, 1 faces, 0 solids (baked)
FEATURE [Part::Revolution] Revolve069  label="removeToCreateScrewAndThreadedInsertHole006"
  Angle = 360
  Axis = (0,1,0)
  Base = (0,0,0)
  FaceMakerClass = Part::FaceMakerBullseye
  Placement = pos=(12.5,0,10) rot=(0,0,1;0rad)
  Solid = false
  Source = -> Face065
  Symmetric = false
FEATURE [Part::Feature] Face066
  shape: bbox 3.5 x 17.8 x 2e-07 mm, 1 faces, 0 solids (baked)
FEATURE [Part::Revolution] Revolve070  label="removeToCreateScrewAndThreadedInsertHole007"
  Angle = 360
  Axis = (0,1,0)
  Base = (0,0,0)
  FaceMakerClass = Part::FaceMakerBullseye
  Placement = pos=(12.5,0,62) rot=(0,0,1;0rad)
  Solid = false
  Source = -> Face066
  Symmetric = false
FEATURE [Part::Feature] Face067
  shape: bbox 3.5 x 17.8 x 2e-07 mm, 1 faces, 0 solids (baked)
FEATURE [Part::Revolution] Revolve071  label="removeToCreateScrewAndThreadedInsertHole008"
  Angle = 360
  Axis = (0,1,0)
  Base = (0,0,0)
  FaceMakerClass = Part::FaceMakerBullseye
  Placement = pos=(89.5,0,68.5) rot=(0,0,1;0rad)
  Solid = false
  Source = -> Face067
  Symmetric = false
FEATURE [Part::Feature] Face068
  shape: bbox 3.5 x 17.8 x 2e-07 mm, 1 faces, 0 solids (baked)
FEATURE [Part::Revolution] Revolve072  label="removeToCreateScrewAndThreadedInsertHole009"
  Angle = 360
  Axis = (0,1,0)
  Base = (0,0,0)
  FaceMakerClass = Part::FaceMakerBullseye
  Placement = pos=(89.5,0,3.5) rot=(0,0,1;0rad)
  Solid = false
  Source = -> Face068
  Symmetric = false
FEATURE [Part::Feature] Face069
  shape: bbox 3.5 x 17.8 x 2e-07 mm, 1 faces, 0 solids (baked)
FEATURE [Part::Feature] Face070
  shape: bbox 3.5 x 17.8 x 2e-07 mm, 1 faces, 0 solids (baked)
FEATURE [Part::Revolution] Revolve073  label="removeToCreateScrewAndThreadedInsertHole010"
  Angle = 360
  Axis = (0,1,0)
  Base = (0,0,0)
  FaceMakerClass = Part::FaceMakerBullseye
  Placement = pos=(102.5,4.7,3.5) rot=(0,0,1;0rad)
  Solid = false
  Source = -> Face069
  Symmetric = false
FEATURE [Part::Revolution] Revolve074  label="removeToCreateScrewAndThreadedInsertHole011"
  Angle = 360
  Axis = (0,1,0)
  Base = (0,0,0)
  FaceMakerClass = Part::FaceMakerBullseye
  Placement = pos=(102.5,4.7,68.5) rot=(0,0,1;0rad)
  Solid = false
  Source = -> Face070
  Symmetric = false
FEATURE [Part::MultiFuse] Fusion048  label="makeHoles001"
  Shapes = -> [Revolve074,Revolve073,Revolve072,Revolve071,Revolve070,Revolve069]
FEATURE [Part::MultiFuse] Fusion049  label="caseScrewRetainers"
  Shapes = -> [Revolve067,Revolve068,Revolve048,Revolve047,Revolve039,Revolve040]
FEATURE [Part::Cut] Cut015  label="caseScrewRetainers001"
  Base = -> Fusion049
  Tool = -> Fusion048
FEATURE [Part::MultiFuse] Fusion050  label="casePillars"
  Shapes = -> [Revolve055,Revolve054,Revolve043,Revolve046,Revolve059,Revolve060]
FEATURE [Part::Feature] Face071 .. Face076  x6 (patterned run collapsed; names and placements below)
  shape: bbox 3.5 x 17.8 x 2e-07 mm, 1 faces, 0 solids (baked)
FEATURE [Part::Revolution] Revolve075  label="removeToCreateScrewAndThreadedInsertHole012"
  Angle = 360
  Axis = (0,1,0)
  Base = (0,0,0)
  FaceMakerClass = Part::FaceMakerBullseye
  Placement = pos=(12.5,0,10) rot=(0,0,1;0rad)
  Solid = false
  Source = -> Face071
  Symmetric = false
FEATURE [Part::Revolution] Revolve076  label="removeToCreateScrewAndThreadedInsertHole013"
  Angle = 360
  Axis = (0,1,0)
  Base = (0,0,0)
  FaceMakerClass = Part::FaceMakerBullseye
  Placement = pos=(12.5,0,62) rot=(0,0,1;0rad)
  Solid = false
  Source = -> Face072
  Symmetric = false
FEATURE [Part::Revolution] Revolve077  label="removeToCreateScrewAndThreadedInsertHole014"
  Angle = 360
  Axis = (0,1,0)
  Base = (0,0,0)
  FaceMakerClass = Part::FaceMakerBullseye
  Placement = pos=(89.5,0,68.5) rot=(0,0,1;0rad)
  Solid = false
  Source = -> Face073
  Symmetric = false
FEATURE [Part::Revolution] Revolve078  label="removeToCreateScrewAndThreadedInsertHole015"
  Angle = 360
  Axis = (0,1,0)
  Base = (0,0,0)
  FaceMakerClass = Part::FaceMakerBullseye
  Placement = pos=(89.5,0,3.5) rot=(0,0,1;0rad)
  Solid = false
  Source = -> Face074
  Symmetric = false
FEATURE [Part::Revolution] Revolve079  label="removeToCreateScrewAndThreadedInsertHole016"
  Angle = 360
  Axis = (0,1,0)
  Base = (0,0,0)
  FaceMakerClass = Part::FaceMakerBullseye
  Placement = pos=(102.5,4.7,3.5) rot=(0,0,1;0rad)
  Solid = false
  Source = -> Face075
  Symmetric = false
FEATURE [Part::Revolution] Revolve080  label="removeToCreateScrewAndThreadedInsertHole017"
  Angle = 360
  Axis = (0,1,0)
  Base = (0,0,0)
  FaceMakerClass = Part::FaceMakerBullseye
  Placement = pos=(102.5,4.7,68.5) rot=(0,0,1;0rad)
  Solid = false
  Source = -> Face076
  Symmetric = false
FEATURE [Part::MultiFuse] Fusion051  label="makeHoles002"
  Shapes = -> [Revolve080,Revolve079,Revolve078,Revolve077,Revolve076,Revolve075]
FEATURE [Part::Cut] Cut016  label="caesPillars"
  Base = -> Fusion050
  Tool = -> Fusion051
FEATURE [Part::Revolution] Revolve009  label="plugHousing016"
  Angle = 360
  Axis = (0,1,0)
  Base = (0,0,0)
  FaceMakerClass = Part::FaceMakerBullseye
  Placement = pos=(0,0,36.15) rot=(0,0,1;0rad)
  Solid = false
  Source = -> Face012
  Symmetric = false
FEATURE [Part::MultiFuse] Fusion014  label="plugHousing023"
  Placement = pos=(0,0,0) rot=(0,0,1;1.5708rad)
  Shapes = -> [Revolve011,Revolve009]
FEATURE [Part::Revolution] Revolve010  label="plugHousing017"
  Angle = 360
  Axis = (0,1,0)
  Base = (0,0,0)
  FaceMakerClass = Part::FaceMakerBullseye
  Placement = pos=(0,0,36.15) rot=(0,0,1;0rad)
  Solid = false
  Source = -> Face014
  Symmetric = false
FEATURE [Part::MultiFuse] Fusion015  label="plugHousing024"
  Placement = pos=(0,0,0) rot=(0,0,1;1.5708rad)
  Shapes = -> [Revolve010,Revolve015]
FEATURE [Part::Revolution] Revolve014  label="plugHousing026"
  Angle = 360
  Axis = (0,1,0)
  Base = (0,0,0)
  FaceMakerClass = Part::FaceMakerBullseye
  Placement = pos=(0,0,36.15) rot=(0,0,1;0rad)
  Solid = false
  Source = -> Face011
  Symmetric = false
FEATURE [Part::Revolution] Revolve013  label="plugHousing025"
  Angle = 360
  Axis = (0,1,0)
  Base = (0,0,0)
  FaceMakerClass = Part::FaceMakerBullseye
  Placement = pos=(0,0,36.15) rot=(0,0,1;0rad)
  Solid = false
  Source = -> Face015
  Symmetric = false
FEATURE [Part::MultiFuse] Fusion016  label="plugHousing028"
  Placement = pos=(0,19,0) rot=(0,0,1;3.14159rad)
  Shapes = -> [Fusion014,Fusion013]
FEATURE [Part::MultiFuse] Fusion011  label="plugHousing018"
  Placement = pos=(0,0,0) rot=(0,0,1;1.5708rad)
  Shapes = -> [Revolve014,Revolve013]
FEATURE [Part::MultiFuse] Fusion012  label="plugHousing019"
  Placement = pos=(0,19,0) rot=(0,0,1;3.14159rad)
  Shapes = -> [Fusion011,Fusion015]
FEATURE [Part::MultiFuse] Fusion017  label="plugHousing029"
  Placement = pos=(122.621,0,-0.15) rot=(0,0,1;0rad)
  Shapes = -> [Fusion016,Fusion012]
FEATURE [Part::MultiFuse] Fusion052  label="casePillarRetainers"
  Shapes = -> [Extrude012,Extrude013,Extrude014,Extrude015,Extrude016,Extrude017,Extrude018,Extrude019,Box011,Box012]
FEATURE [Part::Feature] Face077
  shape: bbox 3.5 x 17.8 x 2e-07 mm, 1 faces, 0 solids (baked)
FEATURE [Part::Revolution] Revolve081  label="removeToCreateScrewAndThreadedInsertHole018"
  Angle = 360
  Axis = (0,1,0)
  Base = (0,0,0)
  FaceMakerClass = Part::FaceMakerBullseye
  Placement = pos=(62.3,30.3,19.7) rot=(0,0,1;0rad)
  Solid = false
  Source = -> Face077
  Symmetric = false
FEATURE [Part::Feature] Face078
  shape: bbox 3.5 x 17.8 x 2e-07 mm, 1 faces, 0 solids (baked)
FEATURE [Part::Revolution] Revolve082  label="removeToCreateScrewAndThreadedInsertHole019"
  Angle = 360
  Axis = (0,1,0)
  Base = (0,0,0)
  FaceMakerClass = Part::FaceMakerBullseye
  Placement = pos=(62.3,30.3,51.7) rot=(0,0,1;0rad)
  Solid = false
  Source = -> Face078
  Symmetric = false
FEATURE [Part::Feature] Face079
  shape: bbox 3.5 x 17.8 x 2e-07 mm, 1 faces, 0 solids (baked)
FEATURE [Part::Revolution] Revolve083  label="removeToCreateScrewAndThreadedInsertHole020"
  Angle = 360
  Axis = (0,1,0)
  Base = (0,0,0)
  FaceMakerClass = Part::FaceMakerBullseye
  Placement = pos=(30.3,30.3,19.7) rot=(0,0,1;0rad)
  Solid = false
  Source = -> Face079
  Symmetric = false
FEATURE [Part::Feature] Face080
  shape: bbox 3.5 x 17.8 x 2e-07 mm, 1 faces, 0 solids (baked)
FEATURE [Part::Revolution] Revolve084  label="removeToCreateScrewAndThreadedInsertHole021"
  Angle = 360
  Axis = (0,1,0)
  Base = (0,0,0)
  FaceMakerClass = Part::FaceMakerBullseye
  Placement = pos=(30.3,30.3,51.7) rot=(0,0,1;0rad)
  Solid = false
  Source = -> Face080
  Symmetric = false
FEATURE [Part::MultiFuse] Fusion053  label="createThreadedInsertHolesForFan"
  Shapes = -> [Revolve081,Revolve082,Revolve083,Revolve084]
FEATURE [Part::Cut] Cut017  label="fanScrewHousing001"
  Base = -> Fusion046
  Tool = -> Fusion053
FEATURE [Part::Feature] Face081
  shape: bbox 3.5 x 17.8 x 2e-07 mm, 1 faces, 0 solids (baked)
FEATURE [Part::Revolution] Revolve085  label="removeToCreateScrewAndThreadedInsertHole022"
  Angle = 360
  Axis = (0,1,0)
  Base = (0,0,0)
  FaceMakerClass = Part::FaceMakerBullseye
  Placement = pos=(62.3,30.3,19.7) rot=(0,0,1;0rad)
  Solid = false
  Source = -> Face081
  Symmetric = false
FEATURE [Part::Feature] Face082
  shape: bbox 3.5 x 17.8 x 2e-07 mm, 1 faces, 0 solids (baked)
FEATURE [Part::Revolution] Revolve086  label="removeToCreateScrewAndThreadedInsertHole023"
  Angle = 360
  Axis = (0,1,0)
  Base = (0,0,0)
  FaceMakerClass = Part::FaceMakerBullseye
  Placement = pos=(62.3,30.3,51.7) rot=(0,0,1;0rad)
  Solid = false
  Source = -> Face082
  Symmetric = false
FEATURE [Part::Feature] Face083
  shape: bbox 3.5 x 17.8 x 2e-07 mm, 1 faces, 0 solids (baked)
FEATURE [Part::Revolution] Revolve087  label="removeToCreateScrewAndThreadedInsertHole024"
  Angle = 360
  Axis = (0,1,0)
  Base = (0,0,0)
  FaceMakerClass = Part::FaceMakerBullseye
  Placement = pos=(30.3,30.3,19.7) rot=(0,0,1;0rad)
  Solid = false
  Source = -> Face083
  Symmetric = false
FEATURE [Part::Feature] Face084
  shape: bbox 3.5 x 17.8 x 2e-07 mm, 1 faces, 0 solids (baked)
FEATURE [Part::Revolution] Revolve088  label="removeToCreateScrewAndThreadedInsertHole025"
  Angle = 360
  Axis = (0,1,0)
  Base = (0,0,0)
  FaceMakerClass = Part::FaceMakerBullseye
  Placement = pos=(30.3,30.3,51.7) rot=(0,0,1;0rad)
  Solid = false
  Source = -> Face084
  Symmetric = false
FEATURE [Part::MultiFuse] Fusion054  label="createThreadedInsertHolesForFan001"
  Shapes = -> [Revolve085,Revolve086,Revolve087,Revolve088]
FEATURE [Part::Cut] Cut018  label="top007"
  Base = -> Fusion040
  Tool = -> Fusion054
FEATURE [Sketcher::SketchObject] Sketch029
  FullyConstrained = false
  Placement = pos=(0,0,0) rot=(1,0,0;1.5708rad)
  sketch-geometry (24):
    g0: ArcOfCircle CenterX=-4 CenterY=-10.5 CenterZ=0 NormalX=0 NormalY=0 NormalZ=1 AngleXU=0 Radius=1.5 StartAngle=6e-16 EndAngle=3.14159
    g1: ArcOfCircle CenterX=-34.2 CenterY=-10.5 CenterZ=0 NormalX=0 NormalY=0 NormalZ=1 AngleXU=0 Radius=1.5 StartAngle=0 EndAngle=3.14159
    g2: ArcOfCircle CenterX=-34.2 CenterY=-27.7 CenterZ=0 NormalX=0 NormalY=0 NormalZ=1 AngleXU=0 Radius=1.5 StartAngle=3.14159 EndAngle=6.28319
    g3: ArcOfCircle CenterX=-4 CenterY=-27.7 CenterZ=0 NormalX=0 NormalY=0 NormalZ=1 AngleXU=0 Radius=1.5 StartAngle=3.1416 EndAngle=6.28319
    g4: ArcOfCircle CenterX=-10 CenterY=-4.3 CenterZ=0 NormalX=0 NormalY=0 NormalZ=1 AngleXU=0 Radius=1.5 StartAngle=2e-16 EndAngle=3.14159
    g5: ArcOfCircle CenterX=-16.1 CenterY=-1.8 CenterZ=0 NormalX=0 NormalY=0 NormalZ=1 AngleXU=0 Radius=1.5 StartAngle=5e-16 EndAngle=3.14159
    g6: ArcOfCircle CenterX=-22.1 CenterY=-1.8 CenterZ=0 NormalX=0 NormalY=0 NormalZ=1 AngleXU=0 Radius=1.5 StartAngle=5e-16 EndAngle=3.14159
    g7: ArcOfCircle CenterX=-28.2 CenterY=-4.3 CenterZ=0 NormalX=0 NormalY=0 NormalZ=1 AngleXU=0 Radius=1.5 StartAngle=2e-16 EndAngle=3.14159
    g8: ArcOfCircle CenterX=-10 CenterY=-33.9 CenterZ=0 NormalX=0 NormalY=0 NormalZ=1 AngleXU=0 Radius=1.5 StartAngle=3.14159 EndAngle=6.28319
    g9: ArcOfCircle CenterX=-16.1 CenterY=-36.4 CenterZ=0 NormalX=0 NormalY=0 NormalZ=1 AngleXU=0 Radius=1.5 StartAngle=3.14159 EndAngle=6.28319
    g10: ArcOfCircle CenterX=-22.1 CenterY=-36.4 CenterZ=0 NormalX=0 NormalY=0 NormalZ=1 AngleXU=0 Radius=1.5 StartAngle=3.14159 EndAngle=6.28319
    g11: ArcOfCircle CenterX=-28.2 CenterY=-33.9 CenterZ=0 NormalX=0 NormalY=0 NormalZ=1 AngleXU=0 Radius=1.5 StartAngle=3.14159 EndAngle=6.28319
    g12: LineSegment StartX=-35.7 StartY=-10.5 StartZ=0 EndX=-35.7 EndY=-27.7 EndZ=0
    g13: LineSegment StartX=-32.7 StartY=-10.5 StartZ=0 EndX=-32.7 EndY=-27.7 EndZ=0
    g14: LineSegment StartX=-29.7 StartY=-33.9 StartZ=0 EndX=-29.7 EndY=-4.3 EndZ=0
    g15: LineSegment StartX=-26.7 StartY=-33.9 StartZ=0 EndX=-26.7 EndY=-4.3 EndZ=0
    g16: LineSegment StartX=-2.5 StartY=-10.5 StartZ=0 EndX=-2.5 EndY=-27.7 EndZ=0
    g17: LineSegment StartX=-8.5 StartY=-4.3 StartZ=0 EndX=-8.5 EndY=-33.9 EndZ=0
    g18: LineSegment StartX=-5.5 StartY=-10.5 StartZ=0 EndX=-5.5 EndY=-27.7 EndZ=0
    g19: LineSegment StartX=-11.5 StartY=-4.3 StartZ=0 EndX=-11.5 EndY=-33.9 EndZ=0
    g20: LineSegment StartX=-14.6 StartY=-1.8 StartZ=0 EndX=-14.6 EndY=-36.4 EndZ=0
    g21: LineSegment StartX=-17.6 StartY=-1.8 StartZ=0 EndX=-17.6 EndY=-36.4 EndZ=0
    g22: LineSegment StartX=-20.6 StartY=-36.4 StartZ=0 EndX=-20.6 EndY=-1.8 EndZ=0
    g23: LineSegment StartX=-23.6 StartY=-1.8 StartZ=0 EndX=-23.6 EndY=-36.4 EndZ=0
  constraints (48):
    c: Block(g0)
    c: Block(g1)
    c: Block(g2)
    c: Block(g3)
    c: Block(g4)
    c: Block(g5)
    c: Block(g6)
    c: Block(g7)
    c: Block(g8)
    c: Block(g9)
    c: Block(g10)
    c: Block(g11)
    c: Coincident(g12,g1)
    c: Coincident(g12,g2)
    c: Vertical(g12)
    c: Coincident(g13,g1)
    c: Coincident(g13,g2)
    c: Vertical(g13)
    c: Coincident(g14,g11)
    c: Coincident(g14,g7)
    c: Vertical(g14)
    c: Coincident(g15,g11)
    c: Coincident(g15,g7)
    c: Vertical(g15)
    c: Coincident(g16,g0)
    c: Coincident(g16,g3)
    c: Vertical(g16)
    c: Coincident(g17,g4)
    c: Coincident(g17,g8)
    c: Vertical(g17)
    c: Coincident(g18,g0)
    c: Coincident(g18,g3)
    c: Vertical(g18)
    c: Coincident(g19,g4)
    c: Coincident(g19,g8)
    c: Vertical(g19)
    c: Coincident(g20,g5)
    c: Coincident(g20,g9)
    c: Vertical(g20)
    c: Coincident(g21,g5)
    c: Coincident(g21,g9)
    c: Vertical(g21)
    c: Coincident(g22,g10)
    c: Coincident(g22,g6)
    c: Vertical(g22)
    c: Coincident(g23,g6)
    c: Coincident(g23,g10)
    c: Vertical(g23)
FEATURE [Part::Extrusion] Extrude020  label="removeToCreateFanGrillHoles"
  Base = -> Sketch029
  Dir = (0,-1,6e-16)
  DirMode = 2
  FaceMakerClass = Part::FaceMakerBullseye
  LengthFwd = 10
  LengthRev = 0
  Placement = pos=(65.4,44,54.82) rot=(0,0,1;0rad)
  Solid = true
  Symmetric = false
FEATURE [Part::MultiFuse] Fusion055  label="top008"
  Shapes = -> [Cut017,Cut018]
FEATURE [Part::Cut] Cut019  label="top009"
  Base = -> Fusion055
  Tool = -> Extrude020
FEATURE [App::MeasureDistance] Distance003  label="Distance: 71.95 mm"
  Distance = 71.9513
  P1 = (117,38,72)
  P2 = (117,38,0.0487319)
FEATURE [Sketcher::SketchObject] Sketch030
  FullyConstrained = true
  Placement = pos=(117,19,0) rot=(0.57735,0.57735,0.57735;2.0944rad)
  sketch-geometry (48):
    g0: LineSegment StartX=-49.19 StartY=69.25 StartZ=0 EndX=-49.19 EndY=66.25 EndZ=0
    g1: LineSegment StartX=-49.19 StartY=63.5 StartZ=0 EndX=-49.19 EndY=60.5 EndZ=0
    g2: LineSegment StartX=-49.19 StartY=57.75 StartZ=0 EndX=-49.19 EndY=54.75 EndZ=0
    g3: LineSegment StartX=-49.19 StartY=52 StartZ=0 EndX=-49.19 EndY=49 EndZ=0
    g4: LineSegment StartX=-49.19 StartY=46.25 StartZ=0 EndX=-49.19 EndY=43.25 EndZ=0
    g5: LineSegment StartX=-49.19 StartY=40.5 StartZ=0 EndX=-49.19 EndY=37.5 EndZ=0
    g6: LineSegment StartX=-49.19 StartY=34.5 StartZ=0 EndX=-49.19 EndY=31.5 EndZ=0
    g7: LineSegment StartX=-49.19 StartY=28.75 StartZ=0 EndX=-49.19 EndY=25.75 EndZ=0
    g8: LineSegment StartX=-49.19 StartY=23 StartZ=0 EndX=-49.19 EndY=20 EndZ=0
    g9: LineSegment StartX=-49.19 StartY=17.25 StartZ=0 EndX=-49.19 EndY=14.25 EndZ=0
    g10: LineSegment StartX=-49.19 StartY=11.5 StartZ=0 EndX=-49.19 EndY=8.5 EndZ=0
    g11: LineSegment StartX=-49.19 StartY=5.75 StartZ=0 EndX=-49.19 EndY=2.75 EndZ=0
    g12: ArcOfCircle CenterX=-1.5 CenterY=67.75 CenterZ=0 NormalX=0 NormalY=0 NormalZ=1 AngleXU=0 Radius=1.5 StartAngle=4.71239 EndAngle=7.85398
    g13: ArcOfCircle CenterX=-1.5 CenterY=62 CenterZ=0 NormalX=0 NormalY=0 NormalZ=1 AngleXU=0 Radius=1.5 StartAngle=4.71239 EndAngle=7.85398
    g14: ArcOfCircle CenterX=-1.5 CenterY=56.25 CenterZ=0 NormalX=0 NormalY=0 NormalZ=1 AngleXU=0 Radius=1.5 StartAngle=4.71239 EndAngle=7.85398
    g15: ArcOfCircle CenterX=-11.49 CenterY=50.5 CenterZ=0 NormalX=0 NormalY=0 NormalZ=1 AngleXU=0 Radius=1.5 StartAngle=4.71239 EndAngle=7.85398
    g16: ArcOfCircle CenterX=-16.28 CenterY=44.75 CenterZ=0 NormalX=0 NormalY=0 NormalZ=1 AngleXU=0 Radius=1.5 StartAngle=4.71239 EndAngle=7.85398
    g17: ArcOfCircle CenterX=-18.2337 CenterY=39 CenterZ=0 NormalX=0 NormalY=0 NormalZ=1 AngleXU=0 Radius=1.5 StartAngle=4.71485 EndAngle=7.85398
    g18: ArcOfCircle CenterX=-16.2837 CenterY=27.25 CenterZ=0 NormalX=0 NormalY=0 NormalZ=1 AngleXU=0 Radius=1.5 StartAngle=4.71485 EndAngle=7.85398
    g19: ArcOfCircle CenterX=-18.2337 CenterY=33 CenterZ=0 NormalX=0 NormalY=0 NormalZ=1 AngleXU=0 Radius=1.5 StartAngle=4.71485 EndAngle=7.85398
    g20: ArcOfCircle CenterX=-11.49 CenterY=21.5 CenterZ=0 NormalX=0 NormalY=0 NormalZ=1 AngleXU=0 Radius=1.5 StartAngle=4.71239 EndAngle=7.85398
    g21: ArcOfCircle CenterX=-1.5 CenterY=4.25 CenterZ=0 NormalX=0 NormalY=0 NormalZ=1 AngleXU=0 Radius=1.5 StartAngle=4.71239 EndAngle=7.85398
    g22: ArcOfCircle CenterX=-1.5 CenterY=10 CenterZ=0 NormalX=0 NormalY=0 NormalZ=1 AngleXU=0 Radius=1.5 StartAngle=4.71239 EndAngle=7.85398
    g23: ArcOfCircle CenterX=-1.5 CenterY=15.75 CenterZ=0 NormalX=0 NormalY=0 NormalZ=1 AngleXU=0 Radius=1.5 StartAngle=4.71239 EndAngle=7.85398
    g24: LineSegment StartX=-49.19 StartY=69.25 StartZ=0 EndX=-1.5 EndY=69.25 EndZ=0
    g25: LineSegment StartX=-49.19 StartY=66.25 StartZ=0 EndX=-1.5 EndY=66.25 EndZ=0
    g26: LineSegment StartX=-49.19 StartY=63.5 StartZ=0 EndX=-1.5 EndY=63.5 EndZ=0
    g27: LineSegment StartX=-49.19 StartY=60.5 StartZ=0 EndX=-1.5 EndY=60.5 EndZ=0
    g28: LineSegment StartX=-49.19 StartY=57.75 StartZ=0 EndX=-1.5 EndY=57.75 EndZ=0
    g29: LineSegment StartX=-49.19 StartY=54.75 StartZ=0 EndX=-1.5 EndY=54.75 EndZ=0
    g30: LineSegment StartX=-49.19 StartY=52 StartZ=0 EndX=-11.49 EndY=52 EndZ=0
    g31: LineSegment StartX=-49.19 StartY=49 StartZ=0 EndX=-11.49 EndY=49 EndZ=0
    g32: LineSegment StartX=-49.19 StartY=46.25 StartZ=0 EndX=-16.28 EndY=46.25 EndZ=0
    g33: LineSegment StartX=-49.19 StartY=43.25 StartZ=0 EndX=-16.28 EndY=43.25 EndZ=0
    g34: LineSegment StartX=-49.19 StartY=40.5 StartZ=0 EndX=-18.2337 EndY=40.5 EndZ=0
    g35: LineSegment StartX=-49.19 StartY=37.5 StartZ=0 EndX=-18.23 EndY=37.5 EndZ=0
    g36: LineSegment StartX=-49.19 StartY=34.5 StartZ=0 EndX=-18.2337 EndY=34.5 EndZ=0
    g37: LineSegment StartX=-49.19 StartY=31.5 StartZ=0 EndX=-18.23 EndY=31.5 EndZ=0
    g38: LineSegment StartX=-49.19 StartY=28.75 StartZ=0 EndX=-16.2837 EndY=28.75 EndZ=0
    g39: LineSegment StartX=-49.19 StartY=25.75 StartZ=0 EndX=-16.28 EndY=25.75 EndZ=0
    g40: LineSegment StartX=-49.19 StartY=23 StartZ=0 EndX=-11.49 EndY=23 EndZ=0
    g41: LineSegment StartX=-49.19 StartY=20 StartZ=0 EndX=-11.49 EndY=20 EndZ=0
    g42: LineSegment StartX=-49.19 StartY=17.25 StartZ=0 EndX=-1.5 EndY=17.25 EndZ=0
    g43: LineSegment StartX=-49.19 StartY=14.25 StartZ=0 EndX=-1.5 EndY=14.25 EndZ=0
    g44: LineSegment StartX=-49.19 StartY=11.5 StartZ=0 EndX=-1.5 EndY=11.5 EndZ=0
    g45: LineSegment StartX=-49.19 StartY=8.5 StartZ=0 EndX=-1.5 EndY=8.5 EndZ=0
    g46: LineSegment StartX=-49.19 StartY=5.75 StartZ=0 EndX=-1.5 EndY=5.75 EndZ=0
    g47: LineSegment StartX=-49.19 StartY=2.75 StartZ=0 EndX=-1.5 EndY=2.75 EndZ=0
  constraints (120):
    c: Vertical(g0)
    c: Distance(g0) = 3
    c: Block(g0)
    c: Vertical(g1)
    c: Distance(g1) = 3
    c: Vertical(g2)
    c: Equal(g0,g2) = 3
    c: Block(g2)
    c: Vertical(g3)
    c: Equal(g1,g3) = 3
    c: Vertical(g4)
    c: Equal(g0,g4) = 3
    c: Block(g4)
    c: Vertical(g5)
    c: Equal(g1,g5) = 3
    c: Vertical(g6)
    c: Equal(g0,g6) = 3
    c: Block(g6)
    c: Vertical(g7)
    c: Equal(g1,g7) = 3
    c: Vertical(g8)
    c: Equal(g0,g8) = 3
    c: Block(g8)
    c: Vertical(g9)
    c: Equal(g1,g9) = 3
    c: Vertical(g10)
    c: Equal(g0,g10) = 3
    c: Block(g10)
    c: Vertical(g11)
    c: Equal(g1,g11) = 3
    c: Block(g12)
    c: Block(g13)
    c: Block(g14)
    c: Block(g15)
    c: Block(g16)
    c: Block(g17)
    c: Block(g18)
    c: Block(g19)
    c: Block(g20)
    c: Block(g21)
    c: Block(g22)
    c: Block(g23)
    c: Block(g11)
    c: Block(g9)
    c: Block(g7)
    c: Block(g5)
    c: Block(g3)
    c: Block(g1)
    c: Coincident(g24,g0)
    c: Coincident(g24,g12)
    c: Horizontal(g24)
    c: Coincident(g25,g0)
    c: Coincident(g25,g12)
    c: Horizontal(g25)
    c: Coincident(g26,g1)
    c: Coincident(g26,g13)
    c: Horizontal(g26)
    c: Coincident(g27,g1)
    c: Coincident(g27,g13)
    c: Horizontal(g27)
    c: Coincident(g28,g2)
    c: Coincident(g28,g14)
    c: Horizontal(g28)
    c: Coincident(g29,g2)
    c: Coincident(g29,g14)
    c: Horizontal(g29)
    c: Coincident(g30,g3)
    c: Coincident(g30,g15)
    c: Horizontal(g30)
    c: Coincident(g31,g3)
    c: Coincident(g31,g15)
    c: Horizontal(g31)
    c: Coincident(g32,g4)
    c: Coincident(g32,g16)
    c: Horizontal(g32)
    c: Coincident(g33,g4)
    c: Coincident(g33,g16)
    c: Horizontal(g33)
    c: Coincident(g34,g5)
    c: Coincident(g34,g17)
    c: Horizontal(g34)
    c: Coincident(g35,g5)
    c: Coincident(g35,g17)
    c: Horizontal(g35)
    c: Coincident(g36,g6)
    c: Coincident(g36,g19)
    c: Horizontal(g36)
    c: Coincident(g37,g6)
    c: Coincident(g37,g19)
    c: Horizontal(g37)
    c: Coincident(g38,g7)
    c: Coincident(g38,g18)
    c: Horizontal(g38)
    c: Coincident(g39,g7)
    c: Coincident(g39,g18)
    c: Horizontal(g39)
    c: Coincident(g40,g8)
    c: Coincident(g40,g20)
    c: Horizontal(g40)
    c: Coincident(g41,g8)
    c: Coincident(g41,g20)
    c: Horizontal(g41)
    c: Coincident(g42,g9)
    c: Coincident(g42,g23)
    c: Horizontal(g42)
    c: Coincident(g43,g9)
    c: Coincident(g43,g23)
    c: Horizontal(g43)
    c: Coincident(g44,g10)
    c: Coincident(g44,g22)
    c: Horizontal(g44)
    c: Coincident(g45,g10)
    c: Coincident(g45,g22)
    c: Horizontal(g45)
    c: Coincident(g46,g11)
    c: Coincident(g46,g21)
    c: Horizontal(g46)
    c: Coincident(g47,g11)
    c: Coincident(g47,g21)
    c: Horizontal(g47)
FEATURE [Sketcher::SketchObject] Sketch031
  FullyConstrained = true
  Placement = pos=(117,19,0) rot=(0.57735,0.57735,0.57735;2.0944rad)
  sketch-geometry (24):
    g0: ArcOfCircle CenterX=-49.19 CenterY=67.75 CenterZ=0 NormalX=0 NormalY=0 NormalZ=1 AngleXU=0 Radius=1.5 StartAngle=1.5708 EndAngle=4.71239
    g1: ArcOfCircle CenterX=-49.19 CenterY=62 CenterZ=0 NormalX=0 NormalY=0 NormalZ=1 AngleXU=0 Radius=1.5 StartAngle=1.5708 EndAngle=4.71239
    g2: ArcOfCircle CenterX=-49.19 CenterY=56.25 CenterZ=0 NormalX=0 NormalY=0 NormalZ=1 AngleXU=0 Radius=1.5 StartAngle=1.5708 EndAngle=4.71239
    g3: ArcOfCircle CenterX=-49.19 CenterY=50.5 CenterZ=0 NormalX=0 NormalY=0 NormalZ=1 AngleXU=0 Radius=1.5 StartAngle=1.5708 EndAngle=4.71239
    g4: ArcOfCircle CenterX=-49.19 CenterY=44.75 CenterZ=0 NormalX=0 NormalY=0 NormalZ=1 AngleXU=0 Radius=1.5 StartAngle=1.5708 EndAngle=4.71239
    g5: ArcOfCircle CenterX=-49.19 CenterY=39 CenterZ=0 NormalX=0 NormalY=0 NormalZ=1 AngleXU=0 Radius=1.5 StartAngle=1.5708 EndAngle=4.71239
    g6: ArcOfCircle CenterX=-49.19 CenterY=33 CenterZ=0 NormalX=0 NormalY=0 NormalZ=1 AngleXU=0 Radius=1.5 StartAngle=1.5708 EndAngle=4.71239
    g7: ArcOfCircle CenterX=-49.19 CenterY=27.25 CenterZ=0 NormalX=0 NormalY=0 NormalZ=1 AngleXU=0 Radius=1.5 StartAngle=1.5708 EndAngle=4.71239
    g8: ArcOfCircle CenterX=-49.19 CenterY=21.5 CenterZ=0 NormalX=0 NormalY=0 NormalZ=1 AngleXU=0 Radius=1.5 StartAngle=1.5708 EndAngle=4.71239
    g9: ArcOfCircle CenterX=-49.19 CenterY=15.75 CenterZ=0 NormalX=0 NormalY=0 NormalZ=1 AngleXU=0 Radius=1.5 StartAngle=1.5708 EndAngle=4.71239
    g10: ArcOfCircle CenterX=-49.19 CenterY=10 CenterZ=0 NormalX=0 NormalY=0 NormalZ=1 AngleXU=0 Radius=1.5 StartAngle=1.5708 EndAngle=4.71239
    g11: ArcOfCircle CenterX=-49.19 CenterY=4.25 CenterZ=0 NormalX=0 NormalY=0 NormalZ=1 AngleXU=0 Radius=1.5 StartAngle=1.5708 EndAngle=4.71239
    g12: LineSegment StartX=-49.19 StartY=69.25 StartZ=0 EndX=-49.19 EndY=66.25 EndZ=0
    g13: LineSegment StartX=-49.19 StartY=63.5 StartZ=0 EndX=-49.19 EndY=60.5 EndZ=0
    g14: LineSegment StartX=-49.19 StartY=57.75 StartZ=0 EndX=-49.19 EndY=54.75 EndZ=0
    g15: LineSegment StartX=-49.19 StartY=52 StartZ=0 EndX=-49.19 EndY=49 EndZ=0
    g16: LineSegment StartX=-49.19 StartY=46.25 StartZ=0 EndX=-49.19 EndY=43.25 EndZ=0
    g17: LineSegment StartX=-49.19 StartY=40.5 StartZ=0 EndX=-49.19 EndY=37.5 EndZ=0
    g18: LineSegment StartX=-49.19 StartY=34.5 StartZ=0 EndX=-49.19 EndY=31.5 EndZ=0
    g19: LineSegment StartX=-49.19 StartY=28.75 StartZ=0 EndX=-49.19 EndY=25.75 EndZ=0
    g20: LineSegment StartX=-49.19 StartY=23 StartZ=0 EndX=-49.19 EndY=20 EndZ=0
    g21: LineSegment StartX=-49.19 StartY=17.25 StartZ=0 EndX=-49.19 EndY=14.25 EndZ=0
    g22: LineSegment StartX=-49.19 StartY=11.5 StartZ=0 EndX=-49.19 EndY=8.5 EndZ=0
    g23: LineSegment StartX=-49.19 StartY=5.75 StartZ=0 EndX=-49.19 EndY=2.75 EndZ=0
  constraints (48):
    c: Block(g0)
    c: Block(g1)
    c: Block(g2)
    c: Block(g3)
    c: Block(g4)
    c: Block(g5)
    c: Block(g6)
    c: Block(g7)
    c: Block(g8)
    c: Block(g9)
    c: Block(g10)
    c: Block(g11)
    c: Coincident(g12,g0)
    c: Coincident(g12,g0)
    c: Vertical(g12)
    c: Vertical(g13)
    c: Coincident(g13,g1)
    c: Vertical(g14)
    c: Coincident(g14,g2)
    c: Vertical(g15)
    c: Coincident(g15,g3)
    c: Vertical(g16)
    c: Coincident(g16,g4)
    c: Vertical(g17)
    c: Coincident(g17,g5)
    c: Vertical(g18)
    c: Coincident(g18,g6)
    c: Vertical(g19)
    c: Coincident(g19,g7)
    c: Vertical(g20)
    c: Coincident(g20,g8)
    c: Vertical(g21)
    c: Coincident(g21,g9)
    c: Vertical(g22)
    c: Coincident(g22,g10)
    c: Vertical(g23)
    c: Coincident(g23,g11)
    c: Block(g23)
    c: Block(g22)
    c: Block(g21)
    c: Block(g20)
    c: Block(g13)
    c: Block(g14)
    c: Block(g15)
    c: Block(g16)
    c: Block(g17)
    c: Block(g18)
    c: Block(g19)
FEATURE [Part::Extrusion] Extrude022
  Base = -> Sketch030
  Dir = (1,-2e-16,2e-16)
  DirMode = 2
  FaceMakerClass = Part::FaceMakerBullseye
  LengthFwd = 19
  LengthRev = 0
  Placement = pos=(-19,0,0) rot=(0,0,1;0rad)
  Solid = true
  Symmetric = false
FEATURE [Part::Fillet] Fillet022
  Base = -> Extrude022
  Edges = 24 edges r=1.49: [Edge6,Edge11,Edge18,Edge23,Edge30,Edge35,Edge42,Edge47,Edge54,Edge59,Edge66,Edge71,Edge78,Edge83,Edge90,Edge95,Edge102,Edge107,Edge114,Edge119,Edge126,Edge131,Edge138,Edge143]
FEATURE [Part::Cut] Cut020  label="top010"
  Base = -> Cut019
  Tool = -> Fillet022
FEATURE [Sketcher::SketchObject] Sketch032
  FullyConstrained = true
  Placement = pos=(117,19,0) rot=(0.57735,0.57735,0.57735;2.0944rad)
  sketch-geometry (48):
    g0: LineSegment StartX=-49.19 StartY=69.25 StartZ=0 EndX=-49.19 EndY=66.25 EndZ=0
    g1: LineSegment StartX=-49.19 StartY=63.5 StartZ=0 EndX=-49.19 EndY=60.5 EndZ=0
    g2: LineSegment StartX=-49.19 StartY=57.75 StartZ=0 EndX=-49.19 EndY=54.75 EndZ=0
    g3: LineSegment StartX=-49.19 StartY=52 StartZ=0 EndX=-49.19 EndY=49 EndZ=0
    g4: LineSegment StartX=-49.19 StartY=46.25 StartZ=0 EndX=-49.19 EndY=43.25 EndZ=0
    g5: LineSegment StartX=-49.19 StartY=40.5 StartZ=0 EndX=-49.19 EndY=37.5 EndZ=0
    g6: LineSegment StartX=-49.19 StartY=34.5 StartZ=0 EndX=-49.19 EndY=31.5 EndZ=0
    g7: LineSegment StartX=-49.19 StartY=28.75 StartZ=0 EndX=-49.19 EndY=25.75 EndZ=0
    g8: LineSegment StartX=-49.19 StartY=23 StartZ=0 EndX=-49.19 EndY=20 EndZ=0
    g9: LineSegment StartX=-49.19 StartY=17.25 StartZ=0 EndX=-49.19 EndY=14.25 EndZ=0
    g10: LineSegment StartX=-49.19 StartY=11.5 StartZ=0 EndX=-49.19 EndY=8.5 EndZ=0
    g11: LineSegment StartX=-49.19 StartY=5.75 StartZ=0 EndX=-49.19 EndY=2.75 EndZ=0
    g12: ArcOfCircle CenterX=-1.5 CenterY=67.75 CenterZ=0 NormalX=0 NormalY=0 NormalZ=1 AngleXU=0 Radius=1.5 StartAngle=4.71239 EndAngle=7.85398
    g13: ArcOfCircle CenterX=-1.5 CenterY=62 CenterZ=0 NormalX=0 NormalY=0 NormalZ=1 AngleXU=0 Radius=1.5 StartAngle=4.71239 EndAngle=7.85398
    g14: ArcOfCircle CenterX=-1.5 CenterY=56.25 CenterZ=0 NormalX=0 NormalY=0 NormalZ=1 AngleXU=0 Radius=1.5 StartAngle=4.71239 EndAngle=7.85398
    g15: ArcOfCircle CenterX=-11.49 CenterY=50.5 CenterZ=0 NormalX=0 NormalY=0 NormalZ=1 AngleXU=0 Radius=1.5 StartAngle=4.71239 EndAngle=7.85398
    g16: ArcOfCircle CenterX=-16.28 CenterY=44.75 CenterZ=0 NormalX=0 NormalY=0 NormalZ=1 AngleXU=0 Radius=1.5 StartAngle=4.71239 EndAngle=7.85398
    g17: ArcOfCircle CenterX=-18.2337 CenterY=39 CenterZ=0 NormalX=0 NormalY=0 NormalZ=1 AngleXU=0 Radius=1.5 StartAngle=4.71485 EndAngle=7.85398
    g18: ArcOfCircle CenterX=-16.2837 CenterY=27.25 CenterZ=0 NormalX=0 NormalY=0 NormalZ=1 AngleXU=0 Radius=1.5 StartAngle=4.71485 EndAngle=7.85398
    g19: ArcOfCircle CenterX=-18.2337 CenterY=33 CenterZ=0 NormalX=0 NormalY=0 NormalZ=1 AngleXU=0 Radius=1.5 StartAngle=4.71485 EndAngle=7.85398
    g20: ArcOfCircle CenterX=-11.49 CenterY=21.5 CenterZ=0 NormalX=0 NormalY=0 NormalZ=1 AngleXU=0 Radius=1.5 StartAngle=4.71239 EndAngle=7.85398
    g21: ArcOfCircle CenterX=-1.5 CenterY=4.25 CenterZ=0 NormalX=0 NormalY=0 NormalZ=1 AngleXU=0 Radius=1.5 StartAngle=4.71239 EndAngle=7.85398
    g22: ArcOfCircle CenterX=-1.5 CenterY=10 CenterZ=0 NormalX=0 NormalY=0 NormalZ=1 AngleXU=0 Radius=1.5 StartAngle=4.71239 EndAngle=7.85398
    g23: ArcOfCircle CenterX=-1.5 CenterY=15.75 CenterZ=0 NormalX=0 NormalY=0 NormalZ=1 AngleXU=0 Radius=1.5 StartAngle=4.71239 EndAngle=7.85398
    g24: LineSegment StartX=-49.19 StartY=69.25 StartZ=0 EndX=-1.5 EndY=69.25 EndZ=0
    g25: LineSegment StartX=-49.19 StartY=66.25 StartZ=0 EndX=-1.5 EndY=66.25 EndZ=0
    g26: LineSegment StartX=-49.19 StartY=63.5 StartZ=0 EndX=-1.5 EndY=63.5 EndZ=0
    g27: LineSegment StartX=-49.19 StartY=60.5 StartZ=0 EndX=-1.5 EndY=60.5 EndZ=0
    g28: LineSegment StartX=-49.19 StartY=57.75 StartZ=0 EndX=-1.5 EndY=57.75 EndZ=0
    g29: LineSegment StartX=-49.19 StartY=54.75 StartZ=0 EndX=-1.5 EndY=54.75 EndZ=0
    g30: LineSegment StartX=-49.19 StartY=52 StartZ=0 EndX=-11.49 EndY=52 EndZ=0
    g31: LineSegment StartX=-49.19 StartY=49 StartZ=0 EndX=-11.49 EndY=49 EndZ=0
    g32: LineSegment StartX=-49.19 StartY=46.25 StartZ=0 EndX=-16.28 EndY=46.25 EndZ=0
    g33: LineSegment StartX=-49.19 StartY=43.25 StartZ=0 EndX=-16.28 EndY=43.25 EndZ=0
    g34: LineSegment StartX=-49.19 StartY=40.5 StartZ=0 EndX=-18.2337 EndY=40.5 EndZ=0
    g35: LineSegment StartX=-49.19 StartY=37.5 StartZ=0 EndX=-18.23 EndY=37.5 EndZ=0
    g36: LineSegment StartX=-49.19 StartY=34.5 StartZ=0 EndX=-18.2337 EndY=34.5 EndZ=0
    g37: LineSegment StartX=-49.19 StartY=31.5 StartZ=0 EndX=-18.23 EndY=31.5 EndZ=0
    g38: LineSegment StartX=-49.19 StartY=28.75 StartZ=0 EndX=-16.2837 EndY=28.75 EndZ=0
    g39: LineSegment StartX=-49.19 StartY=25.75 StartZ=0 EndX=-16.28 EndY=25.75 EndZ=0
    g40: LineSegment StartX=-49.19 StartY=23 StartZ=0 EndX=-11.49 EndY=23 EndZ=0
    g41: LineSegment StartX=-49.19 StartY=20 StartZ=0 EndX=-11.49 EndY=20 EndZ=0
    g42: LineSegment StartX=-49.19 StartY=17.25 StartZ=0 EndX=-1.5 EndY=17.25 EndZ=0
    g43: LineSegment StartX=-49.19 StartY=14.25 StartZ=0 EndX=-1.5 EndY=14.25 EndZ=0
    g44: LineSegment StartX=-49.19 StartY=11.5 StartZ=0 EndX=-1.5 EndY=11.5 EndZ=0
    g45: LineSegment StartX=-49.19 StartY=8.5 StartZ=0 EndX=-1.5 EndY=8.5 EndZ=0
    g46: LineSegment StartX=-49.19 StartY=5.75 StartZ=0 EndX=-1.5 EndY=5.75 EndZ=0
    g47: LineSegment StartX=-49.19 StartY=2.75 StartZ=0 EndX=-1.5 EndY=2.75 EndZ=0
  constraints (120):
    c: Vertical(g0)
    c: Distance(g0) = 3
    c: Block(g0)
    c: Vertical(g1)
    c: Distance(g1) = 3
    c: Vertical(g2)
    c: Equal(g0,g2) = 3
    c: Block(g2)
    c: Vertical(g3)
    c: Equal(g1,g3) = 3
    c: Vertical(g4)
    c: Equal(g0,g4) = 3
    c: Block(g4)
    c: Vertical(g5)
    c: Equal(g1,g5) = 3
    c: Vertical(g6)
    c: Equal(g0,g6) = 3
    c: Block(g6)
    c: Vertical(g7)
    c: Equal(g1,g7) = 3
    c: Vertical(g8)
    c: Equal(g0,g8) = 3
    c: Block(g8)
    c: Vertical(g9)
    c: Equal(g1,g9) = 3
    c: Vertical(g10)
    c: Equal(g0,g10) = 3
    c: Block(g10)
    c: Vertical(g11)
    c: Equal(g1,g11) = 3
    c: Block(g12)
    c: Block(g13)
    c: Block(g14)
    c: Block(g15)
    c: Block(g16)
    c: Block(g17)
    c: Block(g18)
    c: Block(g19)
    c: Block(g20)
    c: Block(g21)
    c: Block(g22)
    c: Block(g23)
    c: Block(g11)
    c: Block(g9)
    c: Block(g7)
    c: Block(g5)
    c: Block(g3)
    c: Block(g1)
    c: Coincident(g24,g0)
    c: Coincident(g24,g12)
    c: Horizontal(g24)
    c: Coincident(g25,g0)
    c: Coincident(g25,g12)
    c: Horizontal(g25)
    c: Coincident(g26,g1)
    c: Coincident(g26,g13)
    c: Horizontal(g26)
    c: Coincident(g27,g1)
    c: Coincident(g27,g13)
    c: Horizontal(g27)
    c: Coincident(g28,g2)
    c: Coincident(g28,g14)
    c: Horizontal(g28)
    c: Coincident(g29,g2)
    c: Coincident(g29,g14)
    c: Horizontal(g29)
    c: Coincident(g30,g3)
    c: Coincident(g30,g15)
    c: Horizontal(g30)
    c: Coincident(g31,g3)
    c: Coincident(g31,g15)
    c: Horizontal(g31)
    c: Coincident(g32,g4)
    c: Coincident(g32,g16)
    c: Horizontal(g32)
    c: Coincident(g33,g4)
    c: Coincident(g33,g16)
    c: Horizontal(g33)
    c: Coincident(g34,g5)
    c: Coincident(g34,g17)
    c: Horizontal(g34)
    c: Coincident(g35,g5)
    c: Coincident(g35,g17)
    c: Horizontal(g35)
    c: Coincident(g36,g6)
    c: Coincident(g36,g19)
    c: Horizontal(g36)
    c: Coincident(g37,g6)
    c: Coincident(g37,g19)
    c: Horizontal(g37)
    c: Coincident(g38,g7)
    c: Coincident(g38,g18)
    c: Horizontal(g38)
    c: Coincident(g39,g7)
    c: Coincident(g39,g18)
    c: Horizontal(g39)
    c: Coincident(g40,g8)
    c: Coincident(g40,g20)
    c: Horizontal(g40)
    c: Coincident(g41,g8)
    c: Coincident(g41,g20)
    c: Horizontal(g41)
    c: Coincident(g42,g9)
    c: Coincident(g42,g23)
    c: Horizontal(g42)
    c: Coincident(g43,g9)
    c: Coincident(g43,g23)
    c: Horizontal(g43)
    c: Coincident(g44,g10)
    c: Coincident(g44,g22)
    c: Horizontal(g44)
    c: Coincident(g45,g10)
    c: Coincident(g45,g22)
    c: Horizontal(g45)
    c: Coincident(g46,g11)
    c: Coincident(g46,g21)
    c: Horizontal(g46)
    c: Coincident(g47,g11)
    c: Coincident(g47,g21)
    c: Horizontal(g47)
FEATURE [Part::Extrusion] Extrude023
  Base = -> Sketch032
  Dir = (1,-2e-16,2e-16)
  DirMode = 2
  FaceMakerClass = Part::FaceMakerBullseye
  LengthFwd = 19
  LengthRev = 0
  Placement = pos=(-19,0,0) rot=(0,0,1;0rad)
  Solid = true
  Symmetric = false
FEATURE [Part::Fillet] Fillet023
  Base = -> Extrude023
  Edges = 24 edges r=1.49: [Edge6,Edge11,Edge18,Edge23,Edge30,Edge35,Edge42,Edge47,Edge54,Edge59,Edge66,Edge71,Edge78,Edge83,Edge90,Edge95,Edge102,Edge107,Edge114,Edge119,Edge126,Edge131,Edge138,Edge143]
  Placement = pos=(0,0.05,0) rot=(0,0,1;0rad)
FEATURE [Part::Cut] Cut014  label="bottom003"
  Base = -> Cut007
  Tool = -> Fusion047
FEATURE [Part::Cut] Cut021
  Base = -> Cut014
  Tool = -> Fillet023
